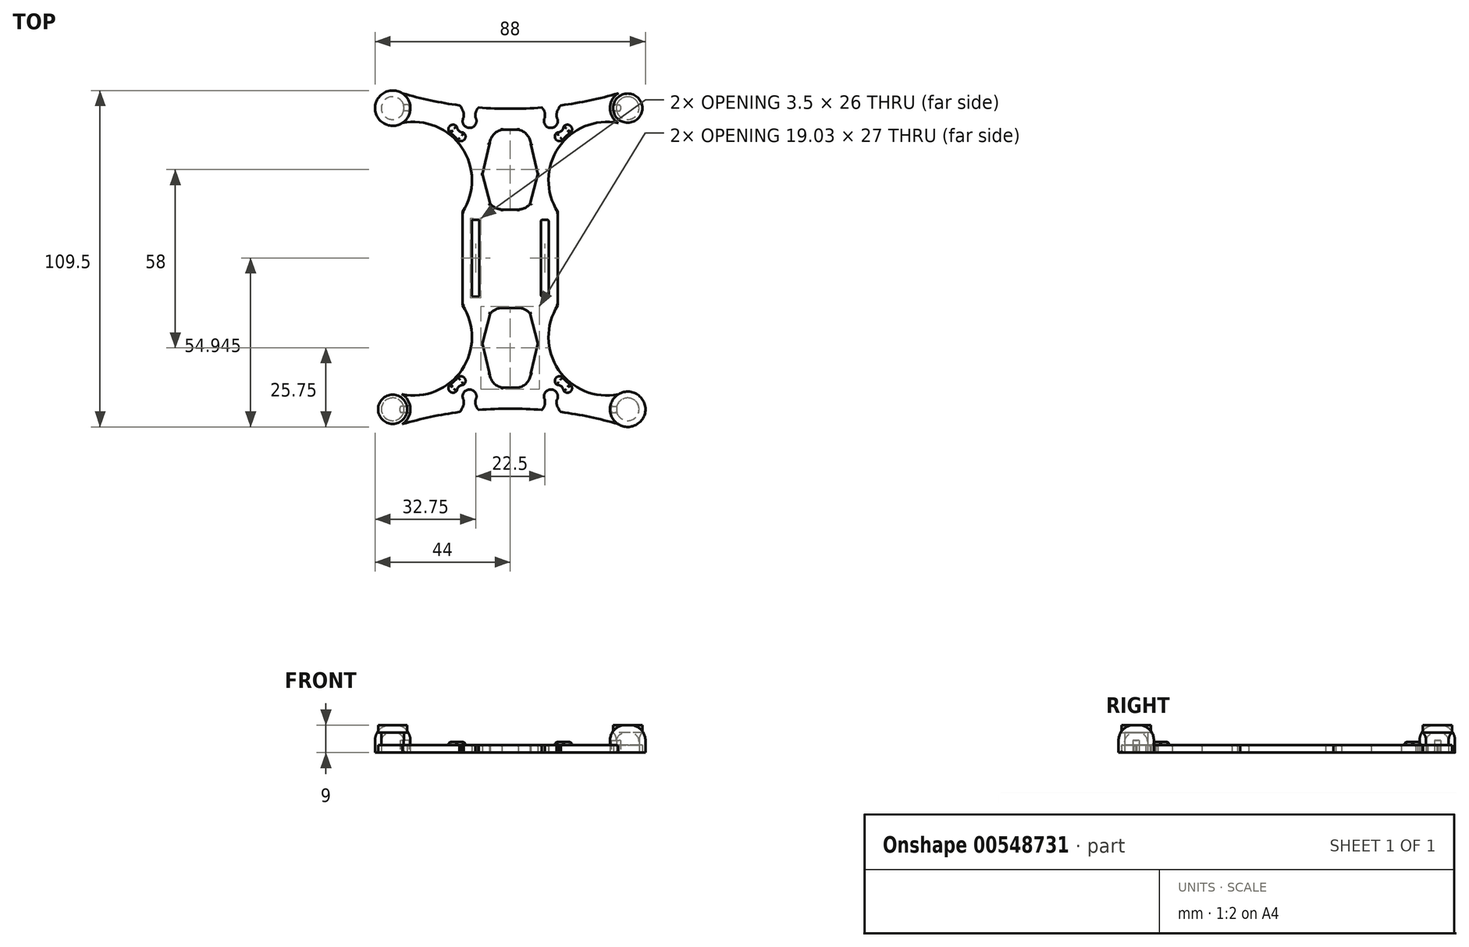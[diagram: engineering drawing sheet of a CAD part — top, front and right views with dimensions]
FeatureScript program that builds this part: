
annotation { "Feature Type Name" : "Feature", "Feature Type Description" : "" }
export const myFeature = defineFeature(function(context is Context, id is Id, definition is map)
    precondition{}
    {
        {
            assignVariable(context, id + "F0", {"name" : "FrameHeight", "anyValue" : 2.5});
        }
        {
            var Q0;
            Q0=qCreatedBy(makeId("Top.planeOp"),FACE);
            var sketch = newSketch(context, id + "F1", { "sketchPlane" : qUnion([Q0])});
            skPoint(sketch, "E0.middle", {"position": v(0, 0) * mm});
            skCircle(sketch, "E1", {"center": v(-38.25, 49) * mm, "radius": 5.75 * mm});
            skCircle(sketch, "E2.MirrorC", {"center": v(38.25, 49) * mm, "radius": 5.75 * mm});
            skCircle(sketch, "E3.MirrorC", {"center": v(-38.25, -49) * mm, "radius": 5.75 * mm});
            skCircle(sketch, "E4.MirrorC", {"center": v(38.25, -49) * mm, "radius": 5.75 * mm});
            skArc(sketch, "E5", {"start": v(-35.12, 53.82) * mm, "mid": v(-25.9, 51.5) * mm, "end": v(-16.55, 49.89) * mm});
            skCircle(sketch, "E6", {"center": v(-38.25, 49) * mm, "radius": 3.7 * mm});
            skCircle(sketch, "E7.MirrorC", {"center": v(38.25, 49) * mm, "radius": 3.7 * mm});
            skCircle(sketch, "E8.MirrorC", {"center": v(38.25, -49) * mm, "radius": 3.7 * mm});
            skCircle(sketch, "E9.MirrorC", {"center": v(-38.25, -49) * mm, "radius": 3.7 * mm});
            skPoint(sketch, "E10.MirrorP", {"position": v(-9, -27.55) * mm});
            skArc(sketch, "E11.MirrorCS", {"start": v(-2.66, -42) * mm, "mid": v(-5.49, -40.33) * mm, "end": v(-6.7, -37.29) * mm});
            skArc(sketch, "E12.MirrorCS", {"start": v(-2.66, -16) * mm, "mid": v(-4.79, -16.51) * mm, "end": v(-6.5, -17.87) * mm});
            skLineSegment(sketch, "E13", {"start": v(-6.5, -17.87) * mm, "end": v(-9, -27.55) * mm});
            skLineSegment(sketch, "E14", {"start": v(-6.7, -37.29) * mm, "end": v(-9, -27.55) * mm});
            skArc(sketch, "E15.MirrorCS", {"start": v(2.66, -16) * mm, "mid": v(4.79, -16.51) * mm, "end": v(6.5, -17.87) * mm});
            skLineSegment(sketch, "E16.MirrorCS", {"start": v(6.5, -17.87) * mm, "end": v(9, -27.55) * mm});
            skLineSegment(sketch, "E17.MirrorCS", {"start": v(6.7, -37.29) * mm, "end": v(9, -27.55) * mm});
            skArc(sketch, "E18.MirrorCS", {"start": v(2.66, -42) * mm, "mid": v(5.49, -40.33) * mm, "end": v(6.7, -37.29) * mm});
            skLineSegment(sketch, "E19", {"start": v(-2.66, -16) * mm, "end": v(2.66, -16) * mm});
            skLineSegment(sketch, "E20", {"start": v(2.66, -42) * mm, "end": v(-2.66, -42) * mm});
            skLineSegment(sketch, "E21.MirrorCS", {"start": v(-2.66, 16) * mm, "end": v(2.66, 16) * mm});
            skArc(sketch, "E22.MirrorCS", {"start": v(-2.66, 16) * mm, "mid": v(-4.79, 16.51) * mm, "end": v(-6.5, 17.87) * mm});
            skLineSegment(sketch, "E23.MirrorCS", {"start": v(-6.5, 17.87) * mm, "end": v(-9, 27.55) * mm});
            skArc(sketch, "E24.MirrorCS", {"start": v(2.66, 16) * mm, "mid": v(4.79, 16.51) * mm, "end": v(6.5, 17.87) * mm});
            skLineSegment(sketch, "E25.MirrorCS", {"start": v(6.5, 17.87) * mm, "end": v(9, 27.55) * mm});
            skLineSegment(sketch, "E26.MirrorCS", {"start": v(-6.7, 37.29) * mm, "end": v(-9, 27.55) * mm});
            skLineSegment(sketch, "E27.MirrorCS", {"start": v(6.7, 37.29) * mm, "end": v(9, 27.55) * mm});
            skArc(sketch, "E28.MirrorCS", {"start": v(2.66, 42) * mm, "mid": v(5.49, 40.33) * mm, "end": v(6.7, 37.29) * mm});
            skLineSegment(sketch, "E29.MirrorCS", {"start": v(2.66, 42) * mm, "end": v(-2.66, 42) * mm});
            skArc(sketch, "E30.MirrorCS", {"start": v(-2.66, 42) * mm, "mid": v(-5.49, 40.33) * mm, "end": v(-6.7, 37.29) * mm});
            skArc(sketch, "E31", {"start": v(-15.5, 15.2) * mm, "mid": v(-15.74, 36.19) * mm, "end": v(-35.17, 44.14) * mm});
            skArc(sketch, "E32.MirrorCS", {"start": v(-35.12, -53.82) * mm, "mid": v(-25.9, -51.5) * mm, "end": v(-16.55, -49.89) * mm});
            skArc(sketch, "E33.MirrorCS", {"start": v(15.5, 15.2) * mm, "mid": v(15.74, 36.19) * mm, "end": v(35.17, 44.14) * mm});
            skArc(sketch, "E34.MirrorCS", {"start": v(15.5, -15.2) * mm, "mid": v(15.74, -36.19) * mm, "end": v(35.17, -44.14) * mm});
            skArc(sketch, "E35.MirrorCS", {"start": v(-15.5, -15.2) * mm, "mid": v(-15.74, -36.19) * mm, "end": v(-35.17, -44.14) * mm});
            skLineSegment(sketch, "E36", {"start": v(-15.5, -15.2) * mm, "end": v(-15.5, 15.2) * mm});
            skLineSegment(sketch, "E37.bottom", {"start": v(-12, -12.3) * mm, "end": v(-10.5, -12.3) * mm});
            skLineSegment(sketch, "E37.top", {"start": v(-12, 12.7) * mm, "end": v(-10.5, 12.7) * mm});
            skLineSegment(sketch, "E37.left", {"start": v(-12.5, -11.8) * mm, "end": v(-12.5, 12.2) * mm});
            skLineSegment(sketch, "E37.right", {"start": v(-10, -11.8) * mm, "end": v(-10, 12.2) * mm});
            skLineSegment(sketch, "E38", {"start": v(-15.5, 15.2) * mm, "end": v(15.5, 15.2) * mm, "construction": true});
            skPoint(sketch, "E39.visualSharp", {"position": v(-10, -12.3) * mm});
            skArc(sketch, "E39.filletArc", {"start": v(-10.5, -12.3) * mm, "mid": v(-10.15, -12.16) * mm, "end": v(-10, -11.8) * mm});
            skPoint(sketch, "E40.visualSharp", {"position": v(-12.5, -12.3) * mm});
            skArc(sketch, "E40.filletArc", {"start": v(-12.5, -11.8) * mm, "mid": v(-12.35, -12.16) * mm, "end": v(-12, -12.3) * mm});
            skPoint(sketch, "E41.visualSharp", {"position": v(-10, 12.7) * mm});
            skArc(sketch, "E41.filletArc", {"start": v(-10, 12.2) * mm, "mid": v(-10.15, 12.55) * mm, "end": v(-10.5, 12.7) * mm});
            skPoint(sketch, "E42.visualSharp", {"position": v(-12.5, 12.7) * mm});
            skArc(sketch, "E42.filletArc", {"start": v(-12, 12.7) * mm, "mid": v(-12.35, 12.55) * mm, "end": v(-12.5, 12.2) * mm});
            skLineSegment(sketch, "E43.MirrorCS", {"start": v(12, -12.3) * mm, "end": v(10.5, -12.3) * mm});
            skArc(sketch, "E44.MirrorCS", {"start": v(12.5, -11.8) * mm, "mid": v(12.35, -12.16) * mm, "end": v(12, -12.3) * mm});
            skArc(sketch, "E45.MirrorCS", {"start": v(10.5, -12.3) * mm, "mid": v(10.15, -12.16) * mm, "end": v(10, -11.8) * mm});
            skLineSegment(sketch, "E46.MirrorCS", {"start": v(10, -11.8) * mm, "end": v(10, 12.2) * mm});
            skLineSegment(sketch, "E47.MirrorCS", {"start": v(12.5, -11.8) * mm, "end": v(12.5, 12.2) * mm});
            skArc(sketch, "E48.MirrorCS", {"start": v(10, 12.2) * mm, "mid": v(10.15, 12.55) * mm, "end": v(10.5, 12.7) * mm});
            skLineSegment(sketch, "E49.MirrorCS", {"start": v(12, 12.7) * mm, "end": v(10.5, 12.7) * mm});
            skArc(sketch, "E50.MirrorCS", {"start": v(12, 12.7) * mm, "mid": v(12.35, 12.55) * mm, "end": v(12.5, 12.2) * mm});
            skLineSegment(sketch, "E51", {"start": v(15.5, 15.2) * mm, "end": v(15.5, -15.2) * mm});
            skArc(sketch, "E52.trimOffspring", {"start": v(-10.28, 49.21) * mm, "mid": v(0, 48.79) * mm, "end": v(10.28, 49.21) * mm});
            skArc(sketch, "E53", {"start": v(-15.18, 45.95) * mm, "mid": v(-13.3, 42.57) * mm, "end": v(-11.24, 45.85) * mm});
            skArc(sketch, "E54", {"start": v(-15.18, 45.95) * mm, "mid": v(-15.18, 47.49) * mm, "end": v(-15.83, 48.88) * mm});
            skArc(sketch, "E55.MirrorCS", {"start": v(-11.24, 45.85) * mm, "mid": v(-11.2, 47.66) * mm, "end": v(-10.28, 49.21) * mm});
            skArc(sketch, "E56.trimOffspring", {"start": v(16.55, 49.89) * mm, "mid": v(25.9, 51.5) * mm, "end": v(35.12, 53.82) * mm});
            skArc(sketch, "E57.trimOffspring", {"start": v(-10.28, -49.21) * mm, "mid": v(0, -48.79) * mm, "end": v(10.28, -49.21) * mm});
            skArc(sketch, "E58.trimOffspring", {"start": v(16.55, -49.89) * mm, "mid": v(25.9, -51.5) * mm, "end": v(35.12, -53.82) * mm});
            skArc(sketch, "E59.MirrorCS", {"start": v(11.24, 45.85) * mm, "mid": v(11.2, 47.66) * mm, "end": v(10.28, 49.21) * mm});
            skArc(sketch, "E60.MirrorCS", {"start": v(15.18, 45.95) * mm, "mid": v(15.18, 47.49) * mm, "end": v(15.83, 48.88) * mm});
            skArc(sketch, "E61.MirrorCS", {"start": v(15.18, 45.95) * mm, "mid": v(13.3, 42.57) * mm, "end": v(11.24, 45.85) * mm});
            skArc(sketch, "E62.MirrorCS", {"start": v(15.18, -45.95) * mm, "mid": v(13.3, -42.57) * mm, "end": v(11.24, -45.85) * mm});
            skArc(sketch, "E63.MirrorCS", {"start": v(11.24, -45.85) * mm, "mid": v(11.2, -47.66) * mm, "end": v(10.28, -49.21) * mm});
            skArc(sketch, "E64.MirrorCS", {"start": v(15.18, -45.95) * mm, "mid": v(15.18, -47.49) * mm, "end": v(15.83, -48.88) * mm});
            skArc(sketch, "E65.MirrorCS", {"start": v(-11.24, -45.85) * mm, "mid": v(-11.2, -47.66) * mm, "end": v(-10.28, -49.21) * mm});
            skArc(sketch, "E66.MirrorCS", {"start": v(-15.18, -45.95) * mm, "mid": v(-15.18, -47.49) * mm, "end": v(-15.83, -48.88) * mm});
            skArc(sketch, "E67.MirrorCS", {"start": v(-15.18, -45.95) * mm, "mid": v(-13.3, -42.57) * mm, "end": v(-11.24, -45.85) * mm});
            skLineSegment(sketch, "E68", {"start": v(-38.25, 49) * mm, "end": v(38.25, 49) * mm, "construction": true});
            skArc(sketch, "E69", {"start": v(16.55, 49.89) * mm, "mid": v(16.05, 49.49) * mm, "end": v(15.83, 48.88) * mm});
            skArc(sketch, "E70.MirrorCS", {"start": v(-16.55, 49.89) * mm, "mid": v(-16.05, 49.49) * mm, "end": v(-15.83, 48.88) * mm});
            skArc(sketch, "E71.MirrorCS", {"start": v(-16.55, -49.89) * mm, "mid": v(-16.05, -49.49) * mm, "end": v(-15.83, -48.88) * mm});
            skArc(sketch, "E72.MirrorCS", {"start": v(16.55, -49.89) * mm, "mid": v(16.05, -49.49) * mm, "end": v(15.83, -48.88) * mm});
            skLineSegment(sketch, "E73", {"start": v(-38.25, -49) * mm, "end": v(38.25, 49) * mm, "construction": true});
            skCircle(sketch, "E74", {"center": v(-38.25, 49) * mm, "radius": 4.75 * mm});
            skCircle(sketch, "E75.MirrorC", {"center": v(38.25, 49) * mm, "radius": 4.75 * mm});
            skCircle(sketch, "E76.MirrorC", {"center": v(38.25, -49) * mm, "radius": 4.75 * mm});
            skCircle(sketch, "E77.MirrorC", {"center": v(-38.25, -49) * mm, "radius": 4.75 * mm});
            skSolve(sketch);
        }
        {
            var Q0;
            {var subQ4=sQuery(id+"F1.wireOp",EDGE,"E5");Q0=makeQuery(id+"F1.imprint","IMPRINT",FACE,{"disambiguationData":[TD([[makeQuery(id+"F1.imprint","IMPRINT",EDGE,{"derivedFrom":subQ4}),-1.0]])]});}
            var Q1;
            Q1=makeQuery(id+"F1.imprint","IMPRINT",FACE,{"disambiguationData":[TD([[makeQuery(id+"F1.imprint","IMPRINT",EDGE,{"derivedFrom":sQuery(id+"F1.wireOp",EDGE,"E9.MirrorC")}),1.0]])]});
            var Q2;
            Q2=makeQuery(id+"F1.imprint","IMPRINT",FACE,{"disambiguationData":[TD([[makeQuery(id+"F1.imprint","IMPRINT",EDGE,{"derivedFrom":sQuery(id+"F1.wireOp",EDGE,"E8.MirrorC")}),-1.0]])]});
            var Q3;
            Q3=makeQuery(id+"F1.imprint","IMPRINT",FACE,{"disambiguationData":[TD([[makeQuery(id+"F1.imprint","IMPRINT",EDGE,{"derivedFrom":sQuery(id+"F1.wireOp",EDGE,"E6")}),-1.0]])]});
            var Q4;
            Q4=makeQuery(id+"F1.imprint","IMPRINT",FACE,{"disambiguationData":[TD([[makeQuery(id+"F1.imprint","IMPRINT",EDGE,{"derivedFrom":sQuery(id+"F1.wireOp",EDGE,"E7.MirrorC")}),1.0]])]});
            var Q5;
            {var subQ0=sQuery(id+"F1.wireOp",EDGE,"7a08c846-7200-404a-ab22-a396ae0e95b40.MirrorCS");Q5=makeQuery(id+"F1.imprint","IMPRINT",FACE,{"disambiguationData":[TD([[makeQuery(id+"F1.imprint","IMPRINT",EDGE,{"derivedFrom":subQ0}),-1.0]])]});}
            extrude(context, id + "F2", {"entities" : qUnion([Q0, Q1, Q2, Q3, Q4, Q5]), "depth" : 2.5 * mm});
        }
        {
            var Q0;
            Q0=makeQuery(id+"F1.imprint","IMPRINT",FACE,{"disambiguationData":[TD([[makeQuery(id+"F1.imprint","IMPRINT",EDGE,{"derivedFrom":sQuery(id+"F1.wireOp",EDGE,"E74")}),-1.0]])]});
            var Q1;
            Q1=makeQuery(id+"F1.imprint","IMPRINT",FACE,{"disambiguationData":[TD([[makeQuery(id+"F1.imprint","IMPRINT",EDGE,{"derivedFrom":sQuery(id+"F1.wireOp",EDGE,"E75.MirrorC")}),1.0]])]});
            var Q2;
            Q2=makeQuery(id+"F1.imprint","IMPRINT",FACE,{"disambiguationData":[TD([[makeQuery(id+"F1.imprint","IMPRINT",EDGE,{"derivedFrom":sQuery(id+"F1.wireOp",EDGE,"E77.MirrorC")}),1.0]])]});
            var Q3;
            Q3=makeQuery(id+"F1.imprint","IMPRINT",FACE,{"disambiguationData":[TD([[makeQuery(id+"F1.imprint","IMPRINT",EDGE,{"derivedFrom":sQuery(id+"F1.wireOp",EDGE,"E76.MirrorC")}),-1.0]])]});
            extrude(context, id + "F3", {"entities" : qUnion([Q0, Q1, Q2, Q3]), "operationType" : NewBodyOperationType.ADD, "depth" : 3 * mm});
        }
        {
            var Q0;
            Q0=makeQuery(id+"F1.imprint","IMPRINT",FACE,{"disambiguationData":[TD([[makeQuery(id+"F1.imprint","IMPRINT",EDGE,{"derivedFrom":sQuery(id+"F1.wireOp",EDGE,"E6")}),-1.0]])]});
            var Q1;
            Q1=makeQuery(id+"F1.imprint","IMPRINT",FACE,{"disambiguationData":[TD([[makeQuery(id+"F1.imprint","IMPRINT",EDGE,{"derivedFrom":sQuery(id+"F1.wireOp",EDGE,"E7.MirrorC")}),1.0]])]});
            var Q2;
            Q2=makeQuery(id+"F1.imprint","IMPRINT",FACE,{"disambiguationData":[TD([[makeQuery(id+"F1.imprint","IMPRINT",EDGE,{"derivedFrom":sQuery(id+"F1.wireOp",EDGE,"E9.MirrorC")}),1.0]])]});
            var Q3;
            Q3=makeQuery(id+"F1.imprint","IMPRINT",FACE,{"disambiguationData":[TD([[makeQuery(id+"F1.imprint","IMPRINT",EDGE,{"derivedFrom":sQuery(id+"F1.wireOp",EDGE,"E8.MirrorC")}),-1.0]])]});
            var Q4;
            Q4=makeQuery(id+"F1.imprint","IMPRINT",FACE,{"disambiguationData":[TD([[makeQuery(id+"F1.imprint","IMPRINT",EDGE,{"derivedFrom":sQuery(id+"F1.wireOp",EDGE,"E6")}),1.0]])]});
            var Q5;
            Q5=makeQuery(id+"F1.imprint","IMPRINT",FACE,{"disambiguationData":[TD([[makeQuery(id+"F1.imprint","IMPRINT",EDGE,{"derivedFrom":sQuery(id+"F1.wireOp",EDGE,"E7.MirrorC")}),-1.0]])]});
            var Q6;
            Q6=makeQuery(id+"F1.imprint","IMPRINT",FACE,{"disambiguationData":[TD([[makeQuery(id+"F1.imprint","IMPRINT",EDGE,{"derivedFrom":sQuery(id+"F1.wireOp",EDGE,"E8.MirrorC")}),1.0]])]});
            var Q7;
            Q7=makeQuery(id+"F1.imprint","IMPRINT",FACE,{"disambiguationData":[TD([[makeQuery(id+"F1.imprint","IMPRINT",EDGE,{"derivedFrom":sQuery(id+"F1.wireOp",EDGE,"E9.MirrorC")}),-1.0]])]});
            var Q8;
            {var subQ0=sQuery(id+"F1.wireOp",EDGE,"ea4f1012-2509-42ab-b6be-2330c5534f0a0.MirrorCS");var subQ1=sQuery(id+"F1.wireOp",EDGE,"cdfdab9b-bf2e-43ec-8392-f97786d2ea0d0.MirrorCS");var subQ2=sQuery(id+"F1.wireOp",EDGE,"465e94d3-5aed-43b1-ab28-4905a897ac150.MirrorCS");var subQ3=sQuery(id+"F1.wireOp",EDGE,"98a759bb-2186-4722-986c-5ad8236f98b60.MirrorCS");var subQ4=sQuery(id+"F1.wireOp",EDGE,"529e4913-d2e2-4b9c-8764-fd74a515156b0.MirrorCS");var subQ5=sQuery(id+"F1.wireOp",EDGE,"a75351e4-8b9f-4b28-a4a3-4962784478ad0.MirrorCS");var subQ6=sQuery(id+"F1.wireOp",EDGE,"82538637-7302-4e28-b2d0-c30d791653240.MirrorCS");var subQ7=sQuery(id+"F1.wireOp",EDGE,"56e68159-8ace-49cd-9e0b-4dd6a05a3e180.MirrorCS");var subQ8=sQuery(id+"F1.wireOp",EDGE,"e7e79bb3-8a2c-4938-af19-8f637f7eba370.MirrorCS");var subQ9=sQuery(id+"F1.wireOp",EDGE,"2316bcf3-3be9-4e9e-b8e2-497a6a1952b90.MirrorCS");var subQ10=sQuery(id+"F1.wireOp",EDGE,"1773aba8-4819-4f46-a8a7-8d94881a3e2a0.MirrorCS");var subQ11=sQuery(id+"F1.wireOp",EDGE,"e0e34dce-b0e1-4d64-a790-8c4829cf73b10.MirrorCS");var subQ12=sQuery(id+"F1.wireOp",EDGE,"8cd6d0e1-198d-4ddf-9674-687771b3d4800.MirrorCS");var subQ13=sQuery(id+"F1.wireOp",EDGE,"258af2fb-57e0-4cd8-8c30-8cafca4a9de30.MirrorCS");var subQ14=sQuery(id+"F1.wireOp",EDGE,"a07b8381-fd63-4e58-856e-6aaff1297d55.filletArc");var subQ15=sQuery(id+"F1.wireOp",EDGE,"RvagwD08-4saL-jRzY-J36Z-niyVwtinKrBz");var subQ16=sQuery(id+"F1.wireOp",EDGE,"o4VfrY1E-f77m-jJ6D-3hSz-oWbsnZmPJ7RM");var subQ17=sQuery(id+"F1.wireOp",EDGE,"5SzH9PIc-MBC3-JWxo-jWJ1-gy0vg8dHxIne");var subQ18=sQuery(id+"F1.wireOp",EDGE,"Skl9KyDn-OFwj-jcuM-sPno-qYqNKXC7fZA3");var subQ19=sQuery(id+"F1.wireOp",EDGE,"5RGUndvU-jcMW-WSWi-Bxv8-2VV6o0UGLXlU");var subQ20=sQuery(id+"F1.wireOp",EDGE,"NKQneA6F-sO9O-ycv6-QC4M-7Sw9j2aKeUUz");var subQ21=sQuery(id+"F1.wireOp",EDGE,"41db651c-dc80-447a-ac2a-c1855a6981c0.filletArc");var subQ22=sQuery(id+"F1.wireOp",EDGE,"cd34b8fd-3b9d-40b5-866b-1931df3bf95f.filletArc");var subQ23=sQuery(id+"F1.wireOp",EDGE,"e2ad8a51-9023-4a85-890f-8adf256902f4.filletArc");var subQ24=sQuery(id+"F1.wireOp",EDGE,"f659aba6-3ceb-4f67-afd8-6bc25f8b2d52.filletArc");var subQ25=sQuery(id+"F1.wireOp",EDGE,"E30.MirrorCS");var subQ26=sQuery(id+"F1.wireOp",EDGE,"E29.MirrorCS");var subQ27=sQuery(id+"F1.wireOp",EDGE,"E28.MirrorCS");var subQ28=sQuery(id+"F1.wireOp",EDGE,"E27.MirrorCS");var subQ29=sQuery(id+"F1.wireOp",EDGE,"E26.MirrorCS");var subQ30=sQuery(id+"F1.wireOp",EDGE,"E25.MirrorCS");var subQ31=sQuery(id+"F1.wireOp",EDGE,"E24.MirrorCS");var subQ32=sQuery(id+"F1.wireOp",EDGE,"E23.MirrorCS");var subQ33=sQuery(id+"F1.wireOp",EDGE,"E22.MirrorCS");var subQ34=sQuery(id+"F1.wireOp",EDGE,"E21.MirrorCS");var subQ35=sQuery(id+"F1.wireOp",EDGE,"E20");var subQ36=sQuery(id+"F1.wireOp",EDGE,"E19");var subQ37=sQuery(id+"F1.wireOp",EDGE,"E18.MirrorCS");var subQ38=sQuery(id+"F1.wireOp",EDGE,"E17.MirrorCS");var subQ39=sQuery(id+"F1.wireOp",EDGE,"E16.MirrorCS");var subQ40=sQuery(id+"F1.wireOp",EDGE,"E15.MirrorCS");var subQ41=sQuery(id+"F1.wireOp",EDGE,"E14");var subQ42=sQuery(id+"F1.wireOp",EDGE,"E13");var subQ43=sQuery(id+"F1.wireOp",EDGE,"E12.MirrorCS");var subQ44=sQuery(id+"F1.wireOp",EDGE,"E11.MirrorCS");var subQ45=sQuery(id+"F1.wireOp",EDGE,"8O0KtBdD-sCAZ-nUyN-ZE4b-Pr8atPqkOLOt.right");var subQ46=sQuery(id+"F1.wireOp",EDGE,"8O0KtBdD-sCAZ-nUyN-ZE4b-Pr8atPqkOLOt.top");var subQ47=sQuery(id+"F1.wireOp",EDGE,"8O0KtBdD-sCAZ-nUyN-ZE4b-Pr8atPqkOLOt.bottom");var subQ48=sQuery(id+"F1.wireOp",EDGE,"3a3e3443-e76c-4b3f-931a-bba0a9ca54bb0.MirrorC");var subQ49=sQuery(id+"F1.wireOp",EDGE,"5ae8c34d-aa19-45d0-b816-4b0481c35e6e0.MirrorC");var subQ50=sQuery(id+"F1.wireOp",EDGE,"e54bd452-817c-44b1-b4a1-4a82a5b737490.MirrorC");var subQ51=sQuery(id+"F1.wireOp",EDGE,"vB4YpJxw-nM1r-KAMU-Z2z7-AA1Xbjjr12VQ");var subQ52=sQuery(id+"F1.wireOp",EDGE,"2126723b-73e3-4daa-88ad-461916ae88fc0.MirrorCS");var subQ53=sQuery(id+"F1.wireOp",EDGE,"8d91ff8a-54ff-47bb-bb8d-6ed09a5a66a50.MirrorCS");var subQ54=sQuery(id+"F1.wireOp",EDGE,"462311f5-9079-46a5-b6e4-7ace82524d020.MirrorCS");var subQ55=sQuery(id+"F1.wireOp",EDGE,"8mwgoKQL-uejJ-Ytzu-yeJP-nfI78MkwDY2L");var subQ56=sQuery(id+"F1.wireOp",EDGE,"3589fe97-52ff-42bc-b7a9-5f631560aecf0.MirrorCS");var subQ57=sQuery(id+"F1.wireOp",EDGE,"E5");var subQ58=sQuery(id+"F1.wireOp",EDGE,"E4.MirrorC");var subQ59=sQuery(id+"F1.wireOp",EDGE,"E3.MirrorC");var subQ60=sQuery(id+"F1.wireOp",EDGE,"E2.MirrorC");var subQ61=sQuery(id+"F1.wireOp",EDGE,"E1");Q8=makeQuery(id+"FTKf5rjYO4gTYV3_1.boolean.opBoolean","MERGE",FACE,{"derivedFrom":[makeQuery(id+"FOrR15PyCScxact_0.opExtrude","CAP_FACE",FACE,{"disambiguationData":[OSD([subQ61,subQ60,subQ59,subQ58,subQ57,subQ56,subQ55,subQ54,subQ53,subQ52,subQ51,subQ50,subQ49,subQ48,subQ47,subQ46,subQ45,subQ44,subQ43,subQ42,subQ41,subQ40,subQ39,subQ38,subQ37,subQ36,subQ35,subQ34,subQ33,subQ32,subQ31,subQ30,subQ29,subQ28,subQ27,subQ26,subQ25,subQ24,subQ23,subQ22,subQ21,subQ20,subQ19,subQ18,subQ17,subQ16,subQ15,subQ14,subQ13,subQ12,subQ11,subQ10,subQ9,subQ8,subQ7,subQ6,subQ5,subQ4,subQ3,subQ2,subQ1,subQ0])],"isStart":false}),makeQuery(id+"FTKf5rjYO4gTYV3_1.opExtrude","CAP_FACE",FACE,{"disambiguationData":[OSD([subQ61,subQ60,subQ59,subQ58,subQ57,subQ56,sQuery(id+"F1.wireOp",EDGE,"E6"),subQ55,subQ54,subQ53,subQ52,sQuery(id+"F1.wireOp",EDGE,"E7.MirrorC"),sQuery(id+"F1.wireOp",EDGE,"E8.MirrorC"),sQuery(id+"F1.wireOp",EDGE,"E9.MirrorC"),subQ51,subQ50,subQ49,subQ48,subQ47,subQ46,subQ45,subQ44,subQ43,subQ42,subQ41,subQ40,subQ39,subQ38,subQ37,subQ36,subQ35,subQ34,subQ33,subQ32,subQ31,subQ30,subQ29,subQ28,subQ27,subQ26,subQ25,subQ24,subQ23,subQ22,subQ21,subQ20,subQ19,subQ18,subQ17,subQ16,subQ15,subQ14,subQ13,subQ12,subQ11,subQ10,subQ9,subQ8,subQ7,subQ6,subQ5,subQ4,subQ3,subQ2,subQ1,subQ0])],"isStart":false})]});}
            var Q9;
            Q9=makeQuery(id+"FOrR15PyCScxact_0.opExtrude","SWEPT_BODY",BODY,{"disambiguationData":[OSD([sQuery(id+"F1.wireOp",EDGE,"E1"),sQuery(id+"F1.wireOp",EDGE,"E2.MirrorC"),sQuery(id+"F1.wireOp",EDGE,"E3.MirrorC"),sQuery(id+"F1.wireOp",EDGE,"E4.MirrorC"),sQuery(id+"F1.wireOp",EDGE,"E5"),sQuery(id+"F1.wireOp",EDGE,"3589fe97-52ff-42bc-b7a9-5f631560aecf0.MirrorCS"),sQuery(id+"F1.wireOp",EDGE,"8mwgoKQL-uejJ-Ytzu-yeJP-nfI78MkwDY2L"),sQuery(id+"F1.wireOp",EDGE,"462311f5-9079-46a5-b6e4-7ace82524d020.MirrorCS"),sQuery(id+"F1.wireOp",EDGE,"8d91ff8a-54ff-47bb-bb8d-6ed09a5a66a50.MirrorCS"),sQuery(id+"F1.wireOp",EDGE,"2126723b-73e3-4daa-88ad-461916ae88fc0.MirrorCS"),sQuery(id+"F1.wireOp",EDGE,"vB4YpJxw-nM1r-KAMU-Z2z7-AA1Xbjjr12VQ"),sQuery(id+"F1.wireOp",EDGE,"e54bd452-817c-44b1-b4a1-4a82a5b737490.MirrorC"),sQuery(id+"F1.wireOp",EDGE,"5ae8c34d-aa19-45d0-b816-4b0481c35e6e0.MirrorC"),sQuery(id+"F1.wireOp",EDGE,"3a3e3443-e76c-4b3f-931a-bba0a9ca54bb0.MirrorC"),sQuery(id+"F1.wireOp",EDGE,"8O0KtBdD-sCAZ-nUyN-ZE4b-Pr8atPqkOLOt.bottom"),sQuery(id+"F1.wireOp",EDGE,"8O0KtBdD-sCAZ-nUyN-ZE4b-Pr8atPqkOLOt.top"),sQuery(id+"F1.wireOp",EDGE,"8O0KtBdD-sCAZ-nUyN-ZE4b-Pr8atPqkOLOt.right"),sQuery(id+"F1.wireOp",EDGE,"E11.MirrorCS"),sQuery(id+"F1.wireOp",EDGE,"E12.MirrorCS"),sQuery(id+"F1.wireOp",EDGE,"E13"),sQuery(id+"F1.wireOp",EDGE,"E14"),sQuery(id+"F1.wireOp",EDGE,"E15.MirrorCS"),sQuery(id+"F1.wireOp",EDGE,"E16.MirrorCS"),sQuery(id+"F1.wireOp",EDGE,"E17.MirrorCS"),sQuery(id+"F1.wireOp",EDGE,"E18.MirrorCS"),sQuery(id+"F1.wireOp",EDGE,"E19"),sQuery(id+"F1.wireOp",EDGE,"E20"),sQuery(id+"F1.wireOp",EDGE,"E21.MirrorCS"),sQuery(id+"F1.wireOp",EDGE,"E22.MirrorCS"),sQuery(id+"F1.wireOp",EDGE,"E23.MirrorCS"),sQuery(id+"F1.wireOp",EDGE,"E24.MirrorCS"),sQuery(id+"F1.wireOp",EDGE,"E25.MirrorCS"),sQuery(id+"F1.wireOp",EDGE,"E26.MirrorCS"),sQuery(id+"F1.wireOp",EDGE,"E27.MirrorCS"),sQuery(id+"F1.wireOp",EDGE,"E28.MirrorCS"),sQuery(id+"F1.wireOp",EDGE,"E29.MirrorCS"),sQuery(id+"F1.wireOp",EDGE,"E30.MirrorCS"),sQuery(id+"F1.wireOp",EDGE,"f659aba6-3ceb-4f67-afd8-6bc25f8b2d52.filletArc"),sQuery(id+"F1.wireOp",EDGE,"e2ad8a51-9023-4a85-890f-8adf256902f4.filletArc"),sQuery(id+"F1.wireOp",EDGE,"cd34b8fd-3b9d-40b5-866b-1931df3bf95f.filletArc"),sQuery(id+"F1.wireOp",EDGE,"41db651c-dc80-447a-ac2a-c1855a6981c0.filletArc"),sQuery(id+"F1.wireOp",EDGE,"NKQneA6F-sO9O-ycv6-QC4M-7Sw9j2aKeUUz"),sQuery(id+"F1.wireOp",EDGE,"5RGUndvU-jcMW-WSWi-Bxv8-2VV6o0UGLXlU"),sQuery(id+"F1.wireOp",EDGE,"Skl9KyDn-OFwj-jcuM-sPno-qYqNKXC7fZA3"),sQuery(id+"F1.wireOp",EDGE,"5SzH9PIc-MBC3-JWxo-jWJ1-gy0vg8dHxIne"),sQuery(id+"F1.wireOp",EDGE,"o4VfrY1E-f77m-jJ6D-3hSz-oWbsnZmPJ7RM"),sQuery(id+"F1.wireOp",EDGE,"RvagwD08-4saL-jRzY-J36Z-niyVwtinKrBz"),sQuery(id+"F1.wireOp",EDGE,"a07b8381-fd63-4e58-856e-6aaff1297d55.filletArc"),sQuery(id+"F1.wireOp",EDGE,"258af2fb-57e0-4cd8-8c30-8cafca4a9de30.MirrorCS"),sQuery(id+"F1.wireOp",EDGE,"8cd6d0e1-198d-4ddf-9674-687771b3d4800.MirrorCS"),sQuery(id+"F1.wireOp",EDGE,"e0e34dce-b0e1-4d64-a790-8c4829cf73b10.MirrorCS"),sQuery(id+"F1.wireOp",EDGE,"1773aba8-4819-4f46-a8a7-8d94881a3e2a0.MirrorCS"),sQuery(id+"F1.wireOp",EDGE,"2316bcf3-3be9-4e9e-b8e2-497a6a1952b90.MirrorCS"),sQuery(id+"F1.wireOp",EDGE,"e7e79bb3-8a2c-4938-af19-8f637f7eba370.MirrorCS"),sQuery(id+"F1.wireOp",EDGE,"56e68159-8ace-49cd-9e0b-4dd6a05a3e180.MirrorCS"),sQuery(id+"F1.wireOp",EDGE,"82538637-7302-4e28-b2d0-c30d791653240.MirrorCS"),sQuery(id+"F1.wireOp",EDGE,"a75351e4-8b9f-4b28-a4a3-4962784478ad0.MirrorCS"),sQuery(id+"F1.wireOp",EDGE,"529e4913-d2e2-4b9c-8764-fd74a515156b0.MirrorCS"),sQuery(id+"F1.wireOp",EDGE,"98a759bb-2186-4722-986c-5ad8236f98b60.MirrorCS"),sQuery(id+"F1.wireOp",EDGE,"465e94d3-5aed-43b1-ab28-4905a897ac150.MirrorCS"),sQuery(id+"F1.wireOp",EDGE,"cdfdab9b-bf2e-43ec-8392-f97786d2ea0d0.MirrorCS"),sQuery(id+"F1.wireOp",EDGE,"ea4f1012-2509-42ab-b6be-2330c5534f0a0.MirrorCS")])]});
            extrude(context, id + "F4", {"entities" : qUnion([Q0, Q1, Q2, Q3, Q4, Q5, Q6, Q7]), "depth" : 9 * mm, "hasSecondDirection" : true, "secondDirectionOppositeDirection" : false, "secondDirectionBoundEntityFace" : qUnion([Q8]), "secondDirectionBoundEntityBody" : qUnion([Q9]), "secondDirectionDepth" : (getVariable(context, 'FrameHeight')) * mm});
        }
        {
            var Q0;
            Q0=makeQuery(id+"F1.imprint","IMPRINT",FACE,{"disambiguationData":[TD([[makeQuery(id+"F1.imprint","IMPRINT",EDGE,{"derivedFrom":sQuery(id+"F1.wireOp",EDGE,"E77.MirrorC")}),1.0]])]});
            var Q1;
            Q1=makeQuery(id+"F1.imprint","IMPRINT",FACE,{"disambiguationData":[TD([[makeQuery(id+"F1.imprint","IMPRINT",EDGE,{"derivedFrom":sQuery(id+"F1.wireOp",EDGE,"E74")}),-1.0]])]});
            var Q2;
            Q2=makeQuery(id+"F1.imprint","IMPRINT",FACE,{"disambiguationData":[TD([[makeQuery(id+"F1.imprint","IMPRINT",EDGE,{"derivedFrom":sQuery(id+"F1.wireOp",EDGE,"E76.MirrorC")}),-1.0]])]});
            var Q3;
            Q3=makeQuery(id+"F1.imprint","IMPRINT",FACE,{"disambiguationData":[TD([[makeQuery(id+"F1.imprint","IMPRINT",EDGE,{"derivedFrom":sQuery(id+"F1.wireOp",EDGE,"E75.MirrorC")}),1.0]])]});
            extrude(context, id + "F5", {"entities" : qUnion([Q0, Q1, Q2, Q3]), "operationType" : NewBodyOperationType.ADD, "depth" : 9 * mm, "hasSecondDirection" : true, "secondDirectionOppositeDirection" : false, "secondDirectionDepth" : 3 * mm});
        }
        {
            var Q0;
            Q0=makeQuery(id+"F1.imprint","IMPRINT",FACE,{"disambiguationData":[TD([[makeQuery(id+"F1.imprint","IMPRINT",EDGE,{"derivedFrom":sQuery(id+"F1.wireOp",EDGE,"E6")}),1.0]])]});
            var Q1;
            Q1=makeQuery(id+"F1.imprint","IMPRINT",FACE,{"disambiguationData":[TD([[makeQuery(id+"F1.imprint","IMPRINT",EDGE,{"derivedFrom":sQuery(id+"F1.wireOp",EDGE,"E7.MirrorC")}),-1.0]])]});
            var Q2;
            Q2=makeQuery(id+"F1.imprint","IMPRINT",FACE,{"disambiguationData":[TD([[makeQuery(id+"F1.imprint","IMPRINT",EDGE,{"derivedFrom":sQuery(id+"F1.wireOp",EDGE,"E9.MirrorC")}),-1.0]])]});
            var Q3;
            Q3=makeQuery(id+"F1.imprint","IMPRINT",FACE,{"disambiguationData":[TD([[makeQuery(id+"F1.imprint","IMPRINT",EDGE,{"derivedFrom":sQuery(id+"F1.wireOp",EDGE,"E8.MirrorC")}),1.0]])]});
            extrude(context, id + "F6", {"entities" : qUnion([Q0, Q1, Q2, Q3]), "operationType" : NewBodyOperationType.REMOVE, "depth" : 6.5 * mm, "hasSecondDirection" : true, "secondDirectionOppositeDirection" : false, "secondDirectionDepth" : 2.5 * mm});
        }
        {
            var Q0;
            Q0=makeQuery(id+"F5.opExtrude","CAP_EDGE",EDGE,{"disambiguationData":[OSD([sQuery(id+"F1.wireOp",EDGE,"E1")])],"isStart":false});
            var Q1;
            Q1=makeQuery(id+"F5.opExtrude","CAP_EDGE",EDGE,{"disambiguationData":[OSD([sQuery(id+"F1.wireOp",EDGE,"E2.MirrorC")])],"isStart":false});
            var Q2;
            Q2=makeQuery(id+"F5.opExtrude","CAP_EDGE",EDGE,{"disambiguationData":[OSD([sQuery(id+"F1.wireOp",EDGE,"E4.MirrorC")])],"isStart":false});
            var Q3;
            Q3=makeQuery(id+"F5.opExtrude","CAP_EDGE",EDGE,{"disambiguationData":[OSD([sQuery(id+"F1.wireOp",EDGE,"E3.MirrorC")])],"isStart":false});
            fillet(context, id + "F7", {"entities" : qUnion([Q0, Q1, Q2, Q3]), "radius" : 5 * mm, "tangentPropagation" : true, "allowEdgeOverflow" : false});
        }
        {
            var Q0;
            Q0=makeQuery(id+"F6.boolean.opBoolean","COPY",EDGE,{"derivedFrom":makeQuery(id+"F6.opExtrude","CAP_EDGE",EDGE,{"disambiguationData":[OSD([sQuery(id+"F1.wireOp",EDGE,"E6")])],"isStart":false})});
            var Q1;
            Q1=makeQuery(id+"F6.boolean.opBoolean","COPY",EDGE,{"derivedFrom":makeQuery(id+"F6.opExtrude","CAP_EDGE",EDGE,{"disambiguationData":[OSD([sQuery(id+"F1.wireOp",EDGE,"E7.MirrorC")])],"isStart":false})});
            var Q2;
            Q2=makeQuery(id+"F6.boolean.opBoolean","COPY",FACE,{"derivedFrom":makeQuery(id+"F6.opExtrude","CAP_FACE",FACE,{"disambiguationData":[OSD([sQuery(id+"F1.wireOp",EDGE,"E8.MirrorC")])],"isStart":false})});
            var Q3;
            Q3=makeQuery(id+"F6.boolean.opBoolean","COPY",FACE,{"derivedFrom":makeQuery(id+"F6.opExtrude","CAP_FACE",FACE,{"disambiguationData":[OSD([sQuery(id+"F1.wireOp",EDGE,"E9.MirrorC")])],"isStart":false})});
            fillet(context, id + "F8", {"entities" : qUnion([Q0, Q1, Q2, Q3]), "radius" : 3 * mm, "tangentPropagation" : true, "allowEdgeOverflow" : false});
        }
        {
            var Q0;
            Q0=makeQuery(id+"F1.imprint","IMPRINT",FACE,{"disambiguationData":[TD([[makeQuery(id+"F1.imprint","IMPRINT",EDGE,{"derivedFrom":sQuery(id+"F1.wireOp",EDGE,"E6")}),-1.0]])]});
            var sketch = newSketch(context, id + "F9", { "sketchPlane" : qUnion([Q0])});
            skLineSegment(sketch, "E78.bottom", {"start": v(-33.4, 50.05) * mm, "end": v(-35.4, 50.05) * mm});
            skLineSegment(sketch, "E78.top", {"start": v(-33.4, 48.05) * mm, "end": v(-35.4, 48.05) * mm});
            skLineSegment(sketch, "E78.left", {"start": v(-32.9, 49.55) * mm, "end": v(-32.9, 48.55) * mm});
            skLineSegment(sketch, "E78.right", {"start": v(-35.9, 49.55) * mm, "end": v(-35.9, 48.55) * mm});
            skPoint(sketch, "E78.middle", {"position": v(-34.4, 49.05) * mm});
            skPoint(sketch, "E79.visualSharp", {"position": v(-32.9, 50.05) * mm});
            skArc(sketch, "E79.filletArc", {"start": v(-32.9, 49.55) * mm, "mid": v(-33.05, 49.9) * mm, "end": v(-33.4, 50.05) * mm});
            skPoint(sketch, "E80.visualSharp", {"position": v(-32.9, 48.05) * mm});
            skArc(sketch, "E80.filletArc", {"start": v(-33.4, 48.05) * mm, "mid": v(-33.05, 48.2) * mm, "end": v(-32.9, 48.55) * mm});
            skPoint(sketch, "E81.visualSharp", {"position": v(-35.9, 48.05) * mm});
            skArc(sketch, "E81.filletArc", {"start": v(-35.9, 48.55) * mm, "mid": v(-35.75, 48.2) * mm, "end": v(-35.4, 48.05) * mm});
            skPoint(sketch, "E82.visualSharp", {"position": v(-35.9, 50.05) * mm});
            skArc(sketch, "E82.filletArc", {"start": v(-35.4, 50.05) * mm, "mid": v(-35.75, 49.9) * mm, "end": v(-35.9, 49.55) * mm});
            skLineSegment(sketch, "E83.MirrorCS", {"start": v(33.4, 48.05) * mm, "end": v(35.4, 48.05) * mm});
            skLineSegment(sketch, "E84.MirrorCS", {"start": v(35.9, 49.55) * mm, "end": v(35.9, 48.55) * mm});
            skLineSegment(sketch, "E85.MirrorCS", {"start": v(33.4, 50.05) * mm, "end": v(35.4, 50.05) * mm});
            skLineSegment(sketch, "E86.MirrorCS", {"start": v(32.9, 49.55) * mm, "end": v(32.9, 48.55) * mm});
            skArc(sketch, "E87.MirrorCS", {"start": v(32.9, 49.55) * mm, "mid": v(33.05, 49.9) * mm, "end": v(33.4, 50.05) * mm});
            skArc(sketch, "E88.MirrorCS", {"start": v(33.4, 48.05) * mm, "mid": v(33.05, 48.2) * mm, "end": v(32.9, 48.55) * mm});
            skArc(sketch, "E89.MirrorCS", {"start": v(35.9, 48.55) * mm, "mid": v(35.75, 48.2) * mm, "end": v(35.4, 48.05) * mm});
            skArc(sketch, "E90.MirrorCS", {"start": v(35.4, 50.05) * mm, "mid": v(35.75, 49.9) * mm, "end": v(35.9, 49.55) * mm});
            skLineSegment(sketch, "E91.MirrorCS", {"start": v(33.4, -48.05) * mm, "end": v(35.4, -48.05) * mm});
            skLineSegment(sketch, "E92.MirrorCS", {"start": v(33.4, -50.05) * mm, "end": v(35.4, -50.05) * mm});
            skLineSegment(sketch, "E93.MirrorCS", {"start": v(32.9, -49.55) * mm, "end": v(32.9, -48.55) * mm});
            skLineSegment(sketch, "E94.MirrorCS", {"start": v(35.9, -49.55) * mm, "end": v(35.9, -48.55) * mm});
            skArc(sketch, "E95.MirrorCS", {"start": v(35.4, -50.05) * mm, "mid": v(35.75, -49.9) * mm, "end": v(35.9, -49.55) * mm});
            skArc(sketch, "E96.MirrorCS", {"start": v(32.9, -49.55) * mm, "mid": v(33.05, -49.9) * mm, "end": v(33.4, -50.05) * mm});
            skArc(sketch, "E97.MirrorCS", {"start": v(33.4, -48.05) * mm, "mid": v(33.05, -48.2) * mm, "end": v(32.9, -48.55) * mm});
            skArc(sketch, "E98.MirrorCS", {"start": v(35.9, -48.55) * mm, "mid": v(35.75, -48.2) * mm, "end": v(35.4, -48.05) * mm});
            skLineSegment(sketch, "E99.MirrorCS", {"start": v(-33.4, -48.05) * mm, "end": v(-35.4, -48.05) * mm});
            skArc(sketch, "E100.MirrorCS", {"start": v(-35.9, -48.55) * mm, "mid": v(-35.75, -48.2) * mm, "end": v(-35.4, -48.05) * mm});
            skLineSegment(sketch, "E101.MirrorCS", {"start": v(-35.9, -49.55) * mm, "end": v(-35.9, -48.55) * mm});
            skArc(sketch, "E102.MirrorCS", {"start": v(-35.4, -50.05) * mm, "mid": v(-35.75, -49.9) * mm, "end": v(-35.9, -49.55) * mm});
            skLineSegment(sketch, "E103.MirrorCS", {"start": v(-33.4, -50.05) * mm, "end": v(-35.4, -50.05) * mm});
            skArc(sketch, "E104.MirrorCS", {"start": v(-32.9, -49.55) * mm, "mid": v(-33.05, -49.9) * mm, "end": v(-33.4, -50.05) * mm});
            skLineSegment(sketch, "E105.MirrorCS", {"start": v(-32.9, -49.55) * mm, "end": v(-32.9, -48.55) * mm});
            skArc(sketch, "E106.MirrorCS", {"start": v(-33.4, -48.05) * mm, "mid": v(-33.05, -48.2) * mm, "end": v(-32.9, -48.55) * mm});
            skSolve(sketch);
        }
        {
            var Q0;
            Q0=qSketchRegion(id+"F9",true);
            extrude(context, id + "F10", {"entities" : qUnion([Q0]), "operationType" : NewBodyOperationType.REMOVE, "depth" : 4 * mm});
        }
        {
            var Q0;
            Q0=makeQuery(id+"F2.opExtrude","CAP_EDGE",EDGE,{"disambiguationData":[OSD([sQuery(id+"F1.wireOp",EDGE,"E23.MirrorCS")])],"isStart":true});
            var Q1;
            Q1=makeQuery(id+"F2.opExtrude","CAP_EDGE",EDGE,{"disambiguationData":[OSD([sQuery(id+"F1.wireOp",EDGE,"E22.MirrorCS")])],"isStart":true});
            var Q2;
            Q2=makeQuery(id+"F2.opExtrude","CAP_EDGE",EDGE,{"disambiguationData":[OSD([sQuery(id+"F1.wireOp",EDGE,"E21.MirrorCS")])],"isStart":true});
            var Q3;
            Q3=makeQuery(id+"F2.opExtrude","CAP_EDGE",EDGE,{"disambiguationData":[OSD([sQuery(id+"F1.wireOp",EDGE,"E25.MirrorCS")])],"isStart":true});
            var Q4;
            Q4=makeQuery(id+"F2.opExtrude","CAP_EDGE",EDGE,{"disambiguationData":[OSD([sQuery(id+"F1.wireOp",EDGE,"E24.MirrorCS")])],"isStart":true});
            var Q5;
            Q5=makeQuery(id+"F2.opExtrude","CAP_EDGE",EDGE,{"disambiguationData":[OSD([sQuery(id+"F1.wireOp",EDGE,"E27.MirrorCS")])],"isStart":true});
            var Q6;
            Q6=makeQuery(id+"F2.opExtrude","CAP_EDGE",EDGE,{"disambiguationData":[OSD([sQuery(id+"F1.wireOp",EDGE,"E26.MirrorCS")])],"isStart":true});
            var Q7;
            Q7=makeQuery(id+"F2.opExtrude","CAP_EDGE",EDGE,{"disambiguationData":[OSD([sQuery(id+"F1.wireOp",EDGE,"E30.MirrorCS")])],"isStart":true});
            var Q8;
            Q8=makeQuery(id+"F2.opExtrude","CAP_EDGE",EDGE,{"disambiguationData":[OSD([sQuery(id+"F1.wireOp",EDGE,"E29.MirrorCS")])],"isStart":true});
            var Q9;
            Q9=makeQuery(id+"F2.opExtrude","CAP_EDGE",EDGE,{"disambiguationData":[OSD([sQuery(id+"F1.wireOp",EDGE,"E28.MirrorCS")])],"isStart":true});
            var Q10;
            Q10=makeQuery(id+"F2.opExtrude","CAP_EDGE",EDGE,{"disambiguationData":[OSD([sQuery(id+"F1.wireOp",EDGE,"E24.MirrorCS")])],"isStart":false});
            var Q11;
            Q11=makeQuery(id+"F2.opExtrude","CAP_EDGE",EDGE,{"disambiguationData":[OSD([sQuery(id+"F1.wireOp",EDGE,"E21.MirrorCS")])],"isStart":false});
            var Q12;
            Q12=makeQuery(id+"F2.opExtrude","CAP_EDGE",EDGE,{"disambiguationData":[OSD([sQuery(id+"F1.wireOp",EDGE,"E22.MirrorCS")])],"isStart":false});
            var Q13;
            Q13=makeQuery(id+"F2.opExtrude","CAP_EDGE",EDGE,{"disambiguationData":[OSD([sQuery(id+"F1.wireOp",EDGE,"E23.MirrorCS")])],"isStart":false});
            var Q14;
            Q14=makeQuery(id+"F2.opExtrude","CAP_EDGE",EDGE,{"disambiguationData":[OSD([sQuery(id+"F1.wireOp",EDGE,"E26.MirrorCS")])],"isStart":false});
            var Q15;
            Q15=makeQuery(id+"F2.opExtrude","CAP_EDGE",EDGE,{"disambiguationData":[OSD([sQuery(id+"F1.wireOp",EDGE,"E30.MirrorCS")])],"isStart":false});
            var Q16;
            Q16=makeQuery(id+"F2.opExtrude","CAP_EDGE",EDGE,{"disambiguationData":[OSD([sQuery(id+"F1.wireOp",EDGE,"E29.MirrorCS")])],"isStart":false});
            var Q17;
            Q17=makeQuery(id+"F2.opExtrude","CAP_EDGE",EDGE,{"disambiguationData":[OSD([sQuery(id+"F1.wireOp",EDGE,"E28.MirrorCS")])],"isStart":false});
            var Q18;
            Q18=makeQuery(id+"F2.opExtrude","CAP_EDGE",EDGE,{"disambiguationData":[OSD([sQuery(id+"F1.wireOp",EDGE,"E27.MirrorCS")])],"isStart":false});
            var Q19;
            Q19=makeQuery(id+"F2.opExtrude","CAP_EDGE",EDGE,{"disambiguationData":[OSD([sQuery(id+"F1.wireOp",EDGE,"E25.MirrorCS")])],"isStart":false});
            var Q20;
            Q20=makeQuery(id+"F2.opExtrude","CAP_EDGE",EDGE,{"disambiguationData":[OSD([sQuery(id+"F1.wireOp",EDGE,"E20")])],"isStart":true});
            var Q21;
            Q21=makeQuery(id+"F2.opExtrude","CAP_EDGE",EDGE,{"disambiguationData":[OSD([sQuery(id+"F1.wireOp",EDGE,"E11.MirrorCS")])],"isStart":true});
            var Q22;
            Q22=makeQuery(id+"F2.opExtrude","CAP_EDGE",EDGE,{"disambiguationData":[OSD([sQuery(id+"F1.wireOp",EDGE,"E14")])],"isStart":true});
            var Q23;
            Q23=makeQuery(id+"F2.opExtrude","CAP_EDGE",EDGE,{"disambiguationData":[OSD([sQuery(id+"F1.wireOp",EDGE,"E13")])],"isStart":true});
            var Q24;
            Q24=makeQuery(id+"F2.opExtrude","CAP_EDGE",EDGE,{"disambiguationData":[OSD([sQuery(id+"F1.wireOp",EDGE,"E12.MirrorCS")])],"isStart":true});
            var Q25;
            Q25=makeQuery(id+"F2.opExtrude","CAP_EDGE",EDGE,{"disambiguationData":[OSD([sQuery(id+"F1.wireOp",EDGE,"E19")])],"isStart":true});
            var Q26;
            Q26=makeQuery(id+"F2.opExtrude","CAP_EDGE",EDGE,{"disambiguationData":[OSD([sQuery(id+"F1.wireOp",EDGE,"E15.MirrorCS")])],"isStart":true});
            var Q27;
            Q27=makeQuery(id+"F2.opExtrude","CAP_EDGE",EDGE,{"disambiguationData":[OSD([sQuery(id+"F1.wireOp",EDGE,"E16.MirrorCS")])],"isStart":true});
            var Q28;
            Q28=makeQuery(id+"F2.opExtrude","CAP_EDGE",EDGE,{"disambiguationData":[OSD([sQuery(id+"F1.wireOp",EDGE,"E17.MirrorCS")])],"isStart":true});
            var Q29;
            Q29=makeQuery(id+"F2.opExtrude","CAP_EDGE",EDGE,{"disambiguationData":[OSD([sQuery(id+"F1.wireOp",EDGE,"E18.MirrorCS")])],"isStart":true});
            var Q30;
            Q30=makeQuery(id+"F2.opExtrude","CAP_EDGE",EDGE,{"disambiguationData":[OSD([sQuery(id+"F1.wireOp",EDGE,"E20")])],"isStart":false});
            var Q31;
            Q31=makeQuery(id+"F2.opExtrude","CAP_EDGE",EDGE,{"disambiguationData":[OSD([sQuery(id+"F1.wireOp",EDGE,"E11.MirrorCS")])],"isStart":false});
            var Q32;
            Q32=makeQuery(id+"F2.opExtrude","CAP_EDGE",EDGE,{"disambiguationData":[OSD([sQuery(id+"F1.wireOp",EDGE,"E14")])],"isStart":false});
            var Q33;
            Q33=makeQuery(id+"F2.opExtrude","CAP_EDGE",EDGE,{"disambiguationData":[OSD([sQuery(id+"F1.wireOp",EDGE,"E13")])],"isStart":false});
            var Q34;
            Q34=makeQuery(id+"F2.opExtrude","CAP_EDGE",EDGE,{"disambiguationData":[OSD([sQuery(id+"F1.wireOp",EDGE,"E18.MirrorCS")])],"isStart":false});
            var Q35;
            Q35=makeQuery(id+"F2.opExtrude","CAP_EDGE",EDGE,{"disambiguationData":[OSD([sQuery(id+"F1.wireOp",EDGE,"E17.MirrorCS")])],"isStart":false});
            var Q36;
            Q36=makeQuery(id+"F2.opExtrude","CAP_EDGE",EDGE,{"disambiguationData":[OSD([sQuery(id+"F1.wireOp",EDGE,"E12.MirrorCS")])],"isStart":false});
            var Q37;
            Q37=makeQuery(id+"F2.opExtrude","CAP_EDGE",EDGE,{"disambiguationData":[OSD([sQuery(id+"F1.wireOp",EDGE,"E19")])],"isStart":false});
            var Q38;
            Q38=makeQuery(id+"F2.opExtrude","CAP_EDGE",EDGE,{"disambiguationData":[OSD([sQuery(id+"F1.wireOp",EDGE,"E15.MirrorCS")])],"isStart":false});
            var Q39;
            Q39=makeQuery(id+"F2.opExtrude","CAP_EDGE",EDGE,{"disambiguationData":[OSD([sQuery(id+"F1.wireOp",EDGE,"E16.MirrorCS")])],"isStart":false});
            fillet(context, id + "F11", {"entities" : qUnion([Q0, Q1, Q2, Q3, Q4, Q5, Q6, Q7, Q8, Q9, Q10, Q11, Q12, Q13, Q14, Q15, Q16, Q17, Q18, Q19, Q20, Q21, Q22, Q23, Q24, Q25, Q26, Q27, Q28, Q29, Q30, Q31, Q32, Q33, Q34, Q35, Q36, Q37, Q38, Q39]), "radius" : .5 * mm, "tangentPropagation" : true, "allowEdgeOverflow" : false});
        }
        {
            var Q0;
            Q0=makeQuery(id+"F2.opExtrude","CAP_EDGE",EDGE,{"disambiguationData":[OSD([sQuery(id+"F1.wireOp",EDGE,"E37.left")])],"isStart":false});
            var Q1;
            Q1=makeQuery(id+"F2.opExtrude","CAP_EDGE",EDGE,{"disambiguationData":[OSD([sQuery(id+"F1.wireOp",EDGE,"E37.right")])],"isStart":false});
            var Q2;
            Q2=makeQuery(id+"F2.opExtrude","CAP_EDGE",EDGE,{"disambiguationData":[OSD([sQuery(id+"F1.wireOp",EDGE,"E46.MirrorCS")])],"isStart":false});
            var Q3;
            Q3=makeQuery(id+"F2.opExtrude","CAP_EDGE",EDGE,{"disambiguationData":[OSD([sQuery(id+"F1.wireOp",EDGE,"E47.MirrorCS")])],"isStart":false});
            var Q4;
            Q4=makeQuery(id+"F2.opExtrude","CAP_EDGE",EDGE,{"disambiguationData":[OSD([sQuery(id+"F1.wireOp",EDGE,"E37.left")])],"isStart":true});
            var Q5;
            Q5=makeQuery(id+"F2.opExtrude","CAP_EDGE",EDGE,{"disambiguationData":[OSD([sQuery(id+"F1.wireOp",EDGE,"E37.right")])],"isStart":true});
            var Q6;
            Q6=makeQuery(id+"F2.opExtrude","CAP_EDGE",EDGE,{"disambiguationData":[OSD([sQuery(id+"F1.wireOp",EDGE,"E46.MirrorCS")])],"isStart":true});
            var Q7;
            Q7=makeQuery(id+"F2.opExtrude","CAP_EDGE",EDGE,{"disambiguationData":[OSD([sQuery(id+"F1.wireOp",EDGE,"E47.MirrorCS")])],"isStart":true});
            fillet(context, id + "F12", {"entities" : qUnion([Q0, Q1, Q2, Q3, Q4, Q5, Q6, Q7]), "radius" : .5 * mm, "tangentPropagation" : true, "allowEdgeOverflow" : false});
        }
        {
            var Q0;
            Q0=makeQuery(id+"F2.opExtrude","CAP_EDGE",EDGE,{"disambiguationData":[OSD([sQuery(id+"F1.wireOp",EDGE,"E9.MirrorC")])],"isStart":true});
            var Q1;
            Q1=makeQuery(id+"F2.opExtrude","CAP_EDGE",EDGE,{"disambiguationData":[OSD([sQuery(id+"F1.wireOp",EDGE,"E8.MirrorC")])],"isStart":true});
            var Q2;
            Q2=makeQuery(id+"F2.opExtrude","CAP_EDGE",EDGE,{"disambiguationData":[OSD([sQuery(id+"F1.wireOp",EDGE,"E7.MirrorC")])],"isStart":true});
            var Q3;
            Q3=makeQuery(id+"F2.opExtrude","CAP_EDGE",EDGE,{"disambiguationData":[OSD([sQuery(id+"F1.wireOp",EDGE,"E6")])],"isStart":true});
            fillet(context, id + "F13", {"entities" : qUnion([Q0, Q1, Q2, Q3]), "radius" : .5 * mm, "tangentPropagation" : true, "allowEdgeOverflow" : false});
        }
        {
            var Q0;
            Q0=makeQuery(id+"F2.opExtrude","CAP_EDGE",EDGE,{"disambiguationData":[OSD([sQuery(id+"F1.wireOp",EDGE,"E36")])],"isStart":false});
            var Q1;
            Q1=makeQuery(id+"F2.opExtrude","CAP_EDGE",EDGE,{"disambiguationData":[OSD([sQuery(id+"F1.wireOp",EDGE,"E31")])],"isStart":false});
            var Q2;
            Q2=makeQuery(id+"F2.opExtrude","CAP_EDGE",EDGE,{"disambiguationData":[OSD([sQuery(id+"F1.wireOp",EDGE,"E5")])],"isStart":false});
            var Q3;
            Q3=makeQuery(id+"F2.opExtrude","CAP_EDGE",EDGE,{"disambiguationData":[OSD([sQuery(id+"F1.wireOp",EDGE,"E52.trimOffspring")])],"isStart":false});
            var Q4;
            Q4=makeQuery(id+"F2.opExtrude","CAP_EDGE",EDGE,{"disambiguationData":[OSD([sQuery(id+"F1.wireOp",EDGE,"E56.trimOffspring")])],"isStart":false});
            var Q5;
            Q5=makeQuery(id+"F2.opExtrude","CAP_EDGE",EDGE,{"disambiguationData":[OSD([sQuery(id+"F1.wireOp",EDGE,"E33.MirrorCS")])],"isStart":false});
            var Q6;
            Q6=makeQuery(id+"F2.opExtrude","CAP_EDGE",EDGE,{"disambiguationData":[OSD([sQuery(id+"F1.wireOp",EDGE,"E51")])],"isStart":false});
            var Q7;
            Q7=makeQuery(id+"F2.opExtrude","CAP_EDGE",EDGE,{"disambiguationData":[OSD([sQuery(id+"F1.wireOp",EDGE,"E35.MirrorCS")])],"isStart":false});
            var Q8;
            Q8=makeQuery(id+"F2.opExtrude","CAP_EDGE",EDGE,{"disambiguationData":[OSD([sQuery(id+"F1.wireOp",EDGE,"E34.MirrorCS")])],"isStart":false});
            var Q9;
            Q9=makeQuery(id+"F2.opExtrude","CAP_EDGE",EDGE,{"disambiguationData":[OSD([sQuery(id+"F1.wireOp",EDGE,"E58.trimOffspring")])],"isStart":false});
            var Q10;
            Q10=makeQuery(id+"F2.opExtrude","CAP_EDGE",EDGE,{"disambiguationData":[OSD([sQuery(id+"F1.wireOp",EDGE,"E57.trimOffspring")])],"isStart":false});
            var Q11;
            Q11=makeQuery(id+"F2.opExtrude","CAP_EDGE",EDGE,{"disambiguationData":[OSD([sQuery(id+"F1.wireOp",EDGE,"E32.MirrorCS")])],"isStart":false});
            var Q12;
            Q12=makeQuery(id+"F2.opExtrude","CAP_EDGE",EDGE,{"disambiguationData":[OSD([sQuery(id+"F1.wireOp",EDGE,"E35.MirrorCS")])],"isStart":true});
            var Q13;
            Q13=makeQuery(id+"F2.opExtrude","CAP_EDGE",EDGE,{"disambiguationData":[OSD([sQuery(id+"F1.wireOp",EDGE,"E32.MirrorCS")])],"isStart":true});
            var Q14;
            Q14=makeQuery(id+"F2.opExtrude","CAP_EDGE",EDGE,{"disambiguationData":[OSD([sQuery(id+"F1.wireOp",EDGE,"E57.trimOffspring")])],"isStart":true});
            var Q15;
            Q15=makeQuery(id+"F2.opExtrude","CAP_EDGE",EDGE,{"disambiguationData":[OSD([sQuery(id+"F1.wireOp",EDGE,"E58.trimOffspring")])],"isStart":true});
            var Q16;
            Q16=makeQuery(id+"F2.opExtrude","CAP_EDGE",EDGE,{"disambiguationData":[OSD([sQuery(id+"F1.wireOp",EDGE,"E3.MirrorC")])],"isStart":true});
            var Q17;
            Q17=makeQuery(id+"F2.opExtrude","CAP_EDGE",EDGE,{"disambiguationData":[OSD([sQuery(id+"F1.wireOp",EDGE,"E34.MirrorCS")])],"isStart":true});
            var Q18;
            Q18=makeQuery(id+"F2.opExtrude","CAP_EDGE",EDGE,{"disambiguationData":[OSD([sQuery(id+"F1.wireOp",EDGE,"E4.MirrorC")])],"isStart":true});
            var Q19;
            {var subQ0=sQuery(id+"F1.wireOp",EDGE,"E37.left");Q19=makeQuery(id+"F12.opFillet","BLEND_EDGE",EDGE,{"blendedFrom":[makeQuery(id+"F2.opExtrude","CAP_EDGE",EDGE,{"disambiguationData":[OSD([subQ0])],"isStart":true}),makeQuery(id+"F2.opExtrude","CAP_FACE",FACE,{"disambiguationData":[OSD([sQuery(id+"F1.wireOp",EDGE,"E1"),sQuery(id+"F1.wireOp",EDGE,"E2.MirrorC"),sQuery(id+"F1.wireOp",EDGE,"E3.MirrorC"),sQuery(id+"F1.wireOp",EDGE,"E4.MirrorC"),sQuery(id+"F1.wireOp",EDGE,"E5"),sQuery(id+"F1.wireOp",EDGE,"E6"),sQuery(id+"F1.wireOp",EDGE,"E7.MirrorC"),sQuery(id+"F1.wireOp",EDGE,"E8.MirrorC"),sQuery(id+"F1.wireOp",EDGE,"E9.MirrorC"),sQuery(id+"F1.wireOp",EDGE,"E11.MirrorCS"),sQuery(id+"F1.wireOp",EDGE,"E12.MirrorCS"),sQuery(id+"F1.wireOp",EDGE,"E13"),sQuery(id+"F1.wireOp",EDGE,"E14"),sQuery(id+"F1.wireOp",EDGE,"E15.MirrorCS"),sQuery(id+"F1.wireOp",EDGE,"E16.MirrorCS"),sQuery(id+"F1.wireOp",EDGE,"E17.MirrorCS"),sQuery(id+"F1.wireOp",EDGE,"E18.MirrorCS"),sQuery(id+"F1.wireOp",EDGE,"E19"),sQuery(id+"F1.wireOp",EDGE,"E20"),sQuery(id+"F1.wireOp",EDGE,"E21.MirrorCS"),sQuery(id+"F1.wireOp",EDGE,"E22.MirrorCS"),sQuery(id+"F1.wireOp",EDGE,"E23.MirrorCS"),sQuery(id+"F1.wireOp",EDGE,"E24.MirrorCS"),sQuery(id+"F1.wireOp",EDGE,"E25.MirrorCS"),sQuery(id+"F1.wireOp",EDGE,"E26.MirrorCS"),sQuery(id+"F1.wireOp",EDGE,"E27.MirrorCS"),sQuery(id+"F1.wireOp",EDGE,"E28.MirrorCS"),sQuery(id+"F1.wireOp",EDGE,"E29.MirrorCS"),sQuery(id+"F1.wireOp",EDGE,"E30.MirrorCS"),sQuery(id+"F1.wireOp",EDGE,"E31"),sQuery(id+"F1.wireOp",EDGE,"E32.MirrorCS"),sQuery(id+"F1.wireOp",EDGE,"E33.MirrorCS"),sQuery(id+"F1.wireOp",EDGE,"E34.MirrorCS"),sQuery(id+"F1.wireOp",EDGE,"E35.MirrorCS"),sQuery(id+"F1.wireOp",EDGE,"E36"),sQuery(id+"F1.wireOp",EDGE,"E37.bottom"),sQuery(id+"F1.wireOp",EDGE,"E37.top"),subQ0,sQuery(id+"F1.wireOp",EDGE,"E37.right"),sQuery(id+"F1.wireOp",EDGE,"E39.filletArc"),sQuery(id+"F1.wireOp",EDGE,"E40.filletArc"),sQuery(id+"F1.wireOp",EDGE,"E41.filletArc"),sQuery(id+"F1.wireOp",EDGE,"E42.filletArc"),sQuery(id+"F1.wireOp",EDGE,"E43.MirrorCS"),sQuery(id+"F1.wireOp",EDGE,"E44.MirrorCS"),sQuery(id+"F1.wireOp",EDGE,"E45.MirrorCS"),sQuery(id+"F1.wireOp",EDGE,"E46.MirrorCS"),sQuery(id+"F1.wireOp",EDGE,"E47.MirrorCS"),sQuery(id+"F1.wireOp",EDGE,"E48.MirrorCS"),sQuery(id+"F1.wireOp",EDGE,"E49.MirrorCS"),sQuery(id+"F1.wireOp",EDGE,"E50.MirrorCS"),sQuery(id+"F1.wireOp",EDGE,"E51"),sQuery(id+"F1.wireOp",EDGE,"E52.trimOffspring"),sQuery(id+"F1.wireOp",EDGE,"E53"),sQuery(id+"F1.wireOp",EDGE,"b30a117b-d75a-4502-b387-7b125c7515d1.trimOffspring"),sQuery(id+"F1.wireOp",EDGE,"E54"),sQuery(id+"F1.wireOp",EDGE,"E55.MirrorCS"),sQuery(id+"F1.wireOp",EDGE,"E56.trimOffspring"),sQuery(id+"F1.wireOp",EDGE,"E57.trimOffspring"),sQuery(id+"F1.wireOp",EDGE,"E58.trimOffspring"),sQuery(id+"F1.wireOp",EDGE,"XfeBEER9-2g1J-kN3v-mQVF-R0Wur47D0a7y"),sQuery(id+"F1.wireOp",EDGE,"cj9tdcR5-JuoR-tGsP-MGoO-S5KOOCOVeEPM"),sQuery(id+"F1.wireOp",EDGE,"E59.MirrorCS"),sQuery(id+"F1.wireOp",EDGE,"E60.MirrorCS"),sQuery(id+"F1.wireOp",EDGE,"c64e98b8-e32c-4987-8556-cb4b40954b380.MirrorCS"),sQuery(id+"F1.wireOp",EDGE,"E61.MirrorCS"),sQuery(id+"F1.wireOp",EDGE,"E62.MirrorCS"),sQuery(id+"F1.wireOp",EDGE,"E63.MirrorCS"),sQuery(id+"F1.wireOp",EDGE,"E64.MirrorCS"),sQuery(id+"F1.wireOp",EDGE,"bcf6c320-8a54-4c53-9ffd-94a113f5b3590.MirrorCS"),sQuery(id+"F1.wireOp",EDGE,"c17ce9da-a2d4-493a-92bd-da0e6258ab510.MirrorCS"),sQuery(id+"F1.wireOp",EDGE,"E65.MirrorCS"),sQuery(id+"F1.wireOp",EDGE,"E66.MirrorCS"),sQuery(id+"F1.wireOp",EDGE,"E67.MirrorCS"),sQuery(id+"F1.wireOp",EDGE,"eab108b2-96d9-45b4-925c-b77b0fad8b6b0.MirrorCS"),sQuery(id+"F1.wireOp",EDGE,"861f5b8e-cbd1-41e1-b2bb-9c07049055a20.MirrorCS")])],"isStart":true})],"blendedInto":[makeQuery(id+"F2.opExtrude","CAP_FACE",FACE,{"disambiguationData":[OSD([sQuery(id+"F1.wireOp",EDGE,"E1"),sQuery(id+"F1.wireOp",EDGE,"E2.MirrorC"),sQuery(id+"F1.wireOp",EDGE,"E3.MirrorC"),sQuery(id+"F1.wireOp",EDGE,"E4.MirrorC"),sQuery(id+"F1.wireOp",EDGE,"E5"),sQuery(id+"F1.wireOp",EDGE,"E6"),sQuery(id+"F1.wireOp",EDGE,"E7.MirrorC"),sQuery(id+"F1.wireOp",EDGE,"E8.MirrorC"),sQuery(id+"F1.wireOp",EDGE,"E9.MirrorC"),sQuery(id+"F1.wireOp",EDGE,"E11.MirrorCS"),sQuery(id+"F1.wireOp",EDGE,"E12.MirrorCS"),sQuery(id+"F1.wireOp",EDGE,"E13"),sQuery(id+"F1.wireOp",EDGE,"E14"),sQuery(id+"F1.wireOp",EDGE,"E15.MirrorCS"),sQuery(id+"F1.wireOp",EDGE,"E16.MirrorCS"),sQuery(id+"F1.wireOp",EDGE,"E17.MirrorCS"),sQuery(id+"F1.wireOp",EDGE,"E18.MirrorCS"),sQuery(id+"F1.wireOp",EDGE,"E19"),sQuery(id+"F1.wireOp",EDGE,"E20"),sQuery(id+"F1.wireOp",EDGE,"E21.MirrorCS"),sQuery(id+"F1.wireOp",EDGE,"E22.MirrorCS"),sQuery(id+"F1.wireOp",EDGE,"E23.MirrorCS"),sQuery(id+"F1.wireOp",EDGE,"E24.MirrorCS"),sQuery(id+"F1.wireOp",EDGE,"E25.MirrorCS"),sQuery(id+"F1.wireOp",EDGE,"E26.MirrorCS"),sQuery(id+"F1.wireOp",EDGE,"E27.MirrorCS"),sQuery(id+"F1.wireOp",EDGE,"E28.MirrorCS"),sQuery(id+"F1.wireOp",EDGE,"E29.MirrorCS"),sQuery(id+"F1.wireOp",EDGE,"E30.MirrorCS"),sQuery(id+"F1.wireOp",EDGE,"E31"),sQuery(id+"F1.wireOp",EDGE,"E32.MirrorCS"),sQuery(id+"F1.wireOp",EDGE,"E33.MirrorCS"),sQuery(id+"F1.wireOp",EDGE,"E34.MirrorCS"),sQuery(id+"F1.wireOp",EDGE,"E35.MirrorCS"),sQuery(id+"F1.wireOp",EDGE,"E36"),sQuery(id+"F1.wireOp",EDGE,"E37.bottom"),sQuery(id+"F1.wireOp",EDGE,"E37.top"),subQ0,sQuery(id+"F1.wireOp",EDGE,"E37.right"),sQuery(id+"F1.wireOp",EDGE,"E39.filletArc"),sQuery(id+"F1.wireOp",EDGE,"E40.filletArc"),sQuery(id+"F1.wireOp",EDGE,"E41.filletArc"),sQuery(id+"F1.wireOp",EDGE,"E42.filletArc"),sQuery(id+"F1.wireOp",EDGE,"E43.MirrorCS"),sQuery(id+"F1.wireOp",EDGE,"E44.MirrorCS"),sQuery(id+"F1.wireOp",EDGE,"E45.MirrorCS"),sQuery(id+"F1.wireOp",EDGE,"E46.MirrorCS"),sQuery(id+"F1.wireOp",EDGE,"E47.MirrorCS"),sQuery(id+"F1.wireOp",EDGE,"E48.MirrorCS"),sQuery(id+"F1.wireOp",EDGE,"E49.MirrorCS"),sQuery(id+"F1.wireOp",EDGE,"E50.MirrorCS"),sQuery(id+"F1.wireOp",EDGE,"E51"),sQuery(id+"F1.wireOp",EDGE,"E52.trimOffspring"),sQuery(id+"F1.wireOp",EDGE,"E53"),sQuery(id+"F1.wireOp",EDGE,"b30a117b-d75a-4502-b387-7b125c7515d1.trimOffspring"),sQuery(id+"F1.wireOp",EDGE,"E54"),sQuery(id+"F1.wireOp",EDGE,"E55.MirrorCS"),sQuery(id+"F1.wireOp",EDGE,"E56.trimOffspring"),sQuery(id+"F1.wireOp",EDGE,"E57.trimOffspring"),sQuery(id+"F1.wireOp",EDGE,"E58.trimOffspring"),sQuery(id+"F1.wireOp",EDGE,"XfeBEER9-2g1J-kN3v-mQVF-R0Wur47D0a7y"),sQuery(id+"F1.wireOp",EDGE,"cj9tdcR5-JuoR-tGsP-MGoO-S5KOOCOVeEPM"),sQuery(id+"F1.wireOp",EDGE,"E59.MirrorCS"),sQuery(id+"F1.wireOp",EDGE,"E60.MirrorCS"),sQuery(id+"F1.wireOp",EDGE,"c64e98b8-e32c-4987-8556-cb4b40954b380.MirrorCS"),sQuery(id+"F1.wireOp",EDGE,"E61.MirrorCS"),sQuery(id+"F1.wireOp",EDGE,"E62.MirrorCS"),sQuery(id+"F1.wireOp",EDGE,"E63.MirrorCS"),sQuery(id+"F1.wireOp",EDGE,"E64.MirrorCS"),sQuery(id+"F1.wireOp",EDGE,"bcf6c320-8a54-4c53-9ffd-94a113f5b3590.MirrorCS"),sQuery(id+"F1.wireOp",EDGE,"c17ce9da-a2d4-493a-92bd-da0e6258ab510.MirrorCS"),sQuery(id+"F1.wireOp",EDGE,"E65.MirrorCS"),sQuery(id+"F1.wireOp",EDGE,"E66.MirrorCS"),sQuery(id+"F1.wireOp",EDGE,"E67.MirrorCS"),sQuery(id+"F1.wireOp",EDGE,"eab108b2-96d9-45b4-925c-b77b0fad8b6b0.MirrorCS"),sQuery(id+"F1.wireOp",EDGE,"861f5b8e-cbd1-41e1-b2bb-9c07049055a20.MirrorCS")])],"isStart":true})]});}
            var Q20;
            Q20=makeQuery(id+"F2.opExtrude","CAP_EDGE",EDGE,{"disambiguationData":[OSD([sQuery(id+"F1.wireOp",EDGE,"E51")])],"isStart":true});
            var Q21;
            Q21=makeQuery(id+"F2.opExtrude","CAP_EDGE",EDGE,{"disambiguationData":[OSD([sQuery(id+"F1.wireOp",EDGE,"E36")])],"isStart":true});
            var Q22;
            Q22=makeQuery(id+"F2.opExtrude","CAP_EDGE",EDGE,{"disambiguationData":[OSD([sQuery(id+"F1.wireOp",EDGE,"E33.MirrorCS")])],"isStart":true});
            var Q23;
            Q23=makeQuery(id+"F2.opExtrude","CAP_EDGE",EDGE,{"disambiguationData":[OSD([sQuery(id+"F1.wireOp",EDGE,"E31")])],"isStart":true});
            var Q24;
            Q24=makeQuery(id+"F2.opExtrude","CAP_EDGE",EDGE,{"disambiguationData":[OSD([sQuery(id+"F1.wireOp",EDGE,"E1")])],"isStart":true});
            var Q25;
            Q25=makeQuery(id+"F2.opExtrude","CAP_EDGE",EDGE,{"disambiguationData":[OSD([sQuery(id+"F1.wireOp",EDGE,"E5")])],"isStart":true});
            var Q26;
            Q26=makeQuery(id+"F2.opExtrude","CAP_EDGE",EDGE,{"disambiguationData":[OSD([sQuery(id+"F1.wireOp",EDGE,"E52.trimOffspring")])],"isStart":true});
            var Q27;
            Q27=makeQuery(id+"F2.opExtrude","CAP_EDGE",EDGE,{"disambiguationData":[OSD([sQuery(id+"F1.wireOp",EDGE,"E56.trimOffspring")])],"isStart":true});
            var Q28;
            Q28=makeQuery(id+"F2.opExtrude","CAP_EDGE",EDGE,{"disambiguationData":[OSD([sQuery(id+"F1.wireOp",EDGE,"E2.MirrorC")])],"isStart":true});
            fillet(context, id + "F14", {"entities" : qUnion([Q0, Q1, Q2, Q3, Q4, Q5, Q6, Q7, Q8, Q9, Q10, Q11, Q12, Q13, Q14, Q15, Q16, Q17, Q18, Q19, Q20, Q21, Q22, Q23, Q24, Q25, Q26, Q27, Q28]), "radius" : .5 * mm, "tangentPropagation" : true, "allowEdgeOverflow" : false});
        }
        {
            var Q0;
            Q0=makeQuery(id+"F2.opExtrude","CAP_FACE",FACE,{"disambiguationData":[OSD([sQuery(id+"F1.wireOp",EDGE,"E1"),sQuery(id+"F1.wireOp",EDGE,"E2.MirrorC"),sQuery(id+"F1.wireOp",EDGE,"E3.MirrorC"),sQuery(id+"F1.wireOp",EDGE,"E4.MirrorC"),sQuery(id+"F1.wireOp",EDGE,"E5"),sQuery(id+"F1.wireOp",EDGE,"E6"),sQuery(id+"F1.wireOp",EDGE,"E7.MirrorC"),sQuery(id+"F1.wireOp",EDGE,"E8.MirrorC"),sQuery(id+"F1.wireOp",EDGE,"E9.MirrorC"),sQuery(id+"F1.wireOp",EDGE,"E11.MirrorCS"),sQuery(id+"F1.wireOp",EDGE,"E12.MirrorCS"),sQuery(id+"F1.wireOp",EDGE,"E13"),sQuery(id+"F1.wireOp",EDGE,"E14"),sQuery(id+"F1.wireOp",EDGE,"E15.MirrorCS"),sQuery(id+"F1.wireOp",EDGE,"E16.MirrorCS"),sQuery(id+"F1.wireOp",EDGE,"E17.MirrorCS"),sQuery(id+"F1.wireOp",EDGE,"E18.MirrorCS"),sQuery(id+"F1.wireOp",EDGE,"E19"),sQuery(id+"F1.wireOp",EDGE,"E20"),sQuery(id+"F1.wireOp",EDGE,"E21.MirrorCS"),sQuery(id+"F1.wireOp",EDGE,"E22.MirrorCS"),sQuery(id+"F1.wireOp",EDGE,"E23.MirrorCS"),sQuery(id+"F1.wireOp",EDGE,"E24.MirrorCS"),sQuery(id+"F1.wireOp",EDGE,"E25.MirrorCS"),sQuery(id+"F1.wireOp",EDGE,"E26.MirrorCS"),sQuery(id+"F1.wireOp",EDGE,"E27.MirrorCS"),sQuery(id+"F1.wireOp",EDGE,"E28.MirrorCS"),sQuery(id+"F1.wireOp",EDGE,"E29.MirrorCS"),sQuery(id+"F1.wireOp",EDGE,"E30.MirrorCS"),sQuery(id+"F1.wireOp",EDGE,"E31"),sQuery(id+"F1.wireOp",EDGE,"E32.MirrorCS"),sQuery(id+"F1.wireOp",EDGE,"E33.MirrorCS"),sQuery(id+"F1.wireOp",EDGE,"E34.MirrorCS"),sQuery(id+"F1.wireOp",EDGE,"E35.MirrorCS"),sQuery(id+"F1.wireOp",EDGE,"E36"),sQuery(id+"F1.wireOp",EDGE,"E37.bottom"),sQuery(id+"F1.wireOp",EDGE,"E37.top"),sQuery(id+"F1.wireOp",EDGE,"E37.left"),sQuery(id+"F1.wireOp",EDGE,"E37.right"),sQuery(id+"F1.wireOp",EDGE,"E39.filletArc"),sQuery(id+"F1.wireOp",EDGE,"E40.filletArc"),sQuery(id+"F1.wireOp",EDGE,"E41.filletArc"),sQuery(id+"F1.wireOp",EDGE,"E42.filletArc"),sQuery(id+"F1.wireOp",EDGE,"E43.MirrorCS"),sQuery(id+"F1.wireOp",EDGE,"E44.MirrorCS"),sQuery(id+"F1.wireOp",EDGE,"E45.MirrorCS"),sQuery(id+"F1.wireOp",EDGE,"E46.MirrorCS"),sQuery(id+"F1.wireOp",EDGE,"E47.MirrorCS"),sQuery(id+"F1.wireOp",EDGE,"E48.MirrorCS"),sQuery(id+"F1.wireOp",EDGE,"E49.MirrorCS"),sQuery(id+"F1.wireOp",EDGE,"E50.MirrorCS"),sQuery(id+"F1.wireOp",EDGE,"E51"),sQuery(id+"F1.wireOp",EDGE,"E52.trimOffspring"),sQuery(id+"F1.wireOp",EDGE,"E53"),sQuery(id+"F1.wireOp",EDGE,"b30a117b-d75a-4502-b387-7b125c7515d1.trimOffspring"),sQuery(id+"F1.wireOp",EDGE,"E54"),sQuery(id+"F1.wireOp",EDGE,"E55.MirrorCS"),sQuery(id+"F1.wireOp",EDGE,"E56.trimOffspring"),sQuery(id+"F1.wireOp",EDGE,"E57.trimOffspring"),sQuery(id+"F1.wireOp",EDGE,"E58.trimOffspring"),sQuery(id+"F1.wireOp",EDGE,"XfeBEER9-2g1J-kN3v-mQVF-R0Wur47D0a7y"),sQuery(id+"F1.wireOp",EDGE,"cj9tdcR5-JuoR-tGsP-MGoO-S5KOOCOVeEPM"),sQuery(id+"F1.wireOp",EDGE,"E59.MirrorCS"),sQuery(id+"F1.wireOp",EDGE,"E60.MirrorCS"),sQuery(id+"F1.wireOp",EDGE,"c64e98b8-e32c-4987-8556-cb4b40954b380.MirrorCS"),sQuery(id+"F1.wireOp",EDGE,"E61.MirrorCS"),sQuery(id+"F1.wireOp",EDGE,"E62.MirrorCS"),sQuery(id+"F1.wireOp",EDGE,"E63.MirrorCS"),sQuery(id+"F1.wireOp",EDGE,"E64.MirrorCS"),sQuery(id+"F1.wireOp",EDGE,"bcf6c320-8a54-4c53-9ffd-94a113f5b3590.MirrorCS"),sQuery(id+"F1.wireOp",EDGE,"c17ce9da-a2d4-493a-92bd-da0e6258ab510.MirrorCS"),sQuery(id+"F1.wireOp",EDGE,"E65.MirrorCS"),sQuery(id+"F1.wireOp",EDGE,"E66.MirrorCS"),sQuery(id+"F1.wireOp",EDGE,"E67.MirrorCS"),sQuery(id+"F1.wireOp",EDGE,"eab108b2-96d9-45b4-925c-b77b0fad8b6b0.MirrorCS"),sQuery(id+"F1.wireOp",EDGE,"861f5b8e-cbd1-41e1-b2bb-9c07049055a20.MirrorCS")])],"isStart":false});
            var sketch = newSketch(context, id + "F15", { "sketchPlane" : qUnion([Q0])});
            skPoint(sketch, "E107", {"position": v(17.08, -38.68) * mm});
            skPoint(sketch, "E108", {"position": v(19.36, -40.8) * mm});
            skArc(sketch, "E109", {"start": v(17.08, -38.68) * mm, "mid": v(18.16, -39.8) * mm, "end": v(19.36, -40.8) * mm});
            skPoint(sketch, "E110", {"position": v(17.34, -42.89) * mm});
            skPoint(sketch, "E111", {"position": v(15.3, -41.07) * mm});
            skArc(sketch, "E112", {"start": v(17.34, -42.89) * mm, "mid": v(16.68, -41.58) * mm, "end": v(15.3, -41.07) * mm});
            skPoint(sketch, "E113.right.end.orphan", {"position": v(13.51, -37.55) * mm});
            skArc(sketch, "E114", {"start": v(17.08, -38.68) * mm, "mid": v(14.83, -38.87) * mm, "end": v(15.3, -41.07) * mm});
            skArc(sketch, "E115", {"start": v(17.34, -42.89) * mm, "mid": v(19.54, -43.3) * mm, "end": v(19.71, -41.08) * mm});
            skPoint(sketch, "E116", {"position": v(19.71, -41.08) * mm});
            skLineSegment(sketch, "E117", {"start": v(19.71, -41.08) * mm, "end": v(19.36, -40.8) * mm});
            skArc(sketch, "E118.MirrorCS", {"start": v(-17.08, -38.68) * mm, "mid": v(-14.83, -38.87) * mm, "end": v(-15.3, -41.07) * mm});
            skArc(sketch, "E119.MirrorCS", {"start": v(-17.08, -38.68) * mm, "mid": v(-18.16, -39.8) * mm, "end": v(-19.36, -40.8) * mm});
            skLineSegment(sketch, "E120.MirrorCS", {"start": v(-19.71, -41.08) * mm, "end": v(-19.36, -40.8) * mm});
            skArc(sketch, "E121.MirrorCS", {"start": v(-17.34, -42.89) * mm, "mid": v(-19.54, -43.3) * mm, "end": v(-19.71, -41.08) * mm});
            skArc(sketch, "E122.MirrorCS", {"start": v(-17.34, -42.89) * mm, "mid": v(-16.68, -41.58) * mm, "end": v(-15.3, -41.07) * mm});
            skArc(sketch, "E123.MirrorCS", {"start": v(-17.08, 38.68) * mm, "mid": v(-14.83, 38.87) * mm, "end": v(-15.3, 41.07) * mm});
            skArc(sketch, "E124.MirrorCS", {"start": v(-17.34, 42.89) * mm, "mid": v(-16.68, 41.58) * mm, "end": v(-15.3, 41.07) * mm});
            skArc(sketch, "E125.MirrorCS", {"start": v(-17.34, 42.89) * mm, "mid": v(-19.54, 43.3) * mm, "end": v(-19.71, 41.08) * mm});
            skArc(sketch, "E126.MirrorCS", {"start": v(-17.08, 38.68) * mm, "mid": v(-18.16, 39.8) * mm, "end": v(-19.36, 40.8) * mm});
            skLineSegment(sketch, "E127.MirrorCS", {"start": v(-19.71, 41.08) * mm, "end": v(-19.36, 40.8) * mm});
            skArc(sketch, "E128.MirrorCS", {"start": v(17.08, 38.68) * mm, "mid": v(18.16, 39.8) * mm, "end": v(19.36, 40.8) * mm});
            skArc(sketch, "E129.MirrorCS", {"start": v(17.08, 38.68) * mm, "mid": v(14.83, 38.87) * mm, "end": v(15.3, 41.07) * mm});
            skArc(sketch, "E130.MirrorCS", {"start": v(17.34, 42.89) * mm, "mid": v(16.68, 41.58) * mm, "end": v(15.3, 41.07) * mm});
            skArc(sketch, "E131.MirrorCS", {"start": v(17.34, 42.89) * mm, "mid": v(19.54, 43.3) * mm, "end": v(19.71, 41.08) * mm});
            skLineSegment(sketch, "E132.MirrorCS", {"start": v(19.71, 41.08) * mm, "end": v(19.36, 40.8) * mm});
            skLineSegment(sketch, "E133", {"start": v(16.68, -41.58) * mm, "end": v(18.16, -39.8) * mm, "construction": true});
            skSolve(sketch);
        }
        {
            var Q0;
            Q0=qSketchRegion(id+"F15",true);
            extrude(context, id + "F16", {"entities" : qUnion([Q0]), "operationType" : NewBodyOperationType.ADD, "depth" : 1 * mm});
        }
        {
            var Q0;
            Q0=makeQuery(id+"F16.opExtrude","CAP_EDGE",EDGE,{"disambiguationData":[OSD([sQuery(id+"F15.wireOp",EDGE,"E112")])],"isStart":false});
            var Q1;
            Q1=makeQuery(id+"F16.opExtrude","CAP_EDGE",EDGE,{"disambiguationData":[OSD([sQuery(id+"F15.wireOp",EDGE,"E114")])],"isStart":false});
            var Q2;
            Q2=makeQuery(id+"F16.opExtrude","CAP_EDGE",EDGE,{"disambiguationData":[OSD([sQuery(id+"F15.wireOp",EDGE,"E109")])],"isStart":false});
            var Q3;
            Q3=makeQuery(id+"F16.opExtrude","CAP_EDGE",EDGE,{"disambiguationData":[OSD([sQuery(id+"F15.wireOp",EDGE,"E115")])],"isStart":false});
            var Q4;
            Q4=makeQuery(id+"F16.opExtrude","CAP_EDGE",EDGE,{"disambiguationData":[OSD([sQuery(id+"F15.wireOp",EDGE,"E117")])],"isStart":false});
            var Q5;
            Q5=makeQuery(id+"F16.opExtrude","CAP_EDGE",EDGE,{"disambiguationData":[OSD([sQuery(id+"F15.wireOp",EDGE,"E121.MirrorCS")])],"isStart":false});
            var Q6;
            Q6=makeQuery(id+"F16.opExtrude","CAP_EDGE",EDGE,{"disambiguationData":[OSD([sQuery(id+"F15.wireOp",EDGE,"E122.MirrorCS")])],"isStart":false});
            var Q7;
            Q7=makeQuery(id+"F16.opExtrude","CAP_EDGE",EDGE,{"disambiguationData":[OSD([sQuery(id+"F15.wireOp",EDGE,"E118.MirrorCS")])],"isStart":false});
            var Q8;
            Q8=makeQuery(id+"F16.opExtrude","CAP_EDGE",EDGE,{"disambiguationData":[OSD([sQuery(id+"F15.wireOp",EDGE,"E119.MirrorCS")])],"isStart":false});
            var Q9;
            Q9=makeQuery(id+"F16.opExtrude","CAP_EDGE",EDGE,{"disambiguationData":[OSD([sQuery(id+"F15.wireOp",EDGE,"E120.MirrorCS")])],"isStart":false});
            var Q10;
            Q10=makeQuery(id+"F16.opExtrude","CAP_EDGE",EDGE,{"disambiguationData":[OSD([sQuery(id+"F15.wireOp",EDGE,"E126.MirrorCS")])],"isStart":false});
            var Q11;
            Q11=makeQuery(id+"F16.opExtrude","CAP_EDGE",EDGE,{"disambiguationData":[OSD([sQuery(id+"F15.wireOp",EDGE,"E127.MirrorCS")])],"isStart":false});
            var Q12;
            Q12=makeQuery(id+"F16.opExtrude","CAP_EDGE",EDGE,{"disambiguationData":[OSD([sQuery(id+"F15.wireOp",EDGE,"E125.MirrorCS")])],"isStart":false});
            var Q13;
            Q13=makeQuery(id+"F16.opExtrude","CAP_EDGE",EDGE,{"disambiguationData":[OSD([sQuery(id+"F15.wireOp",EDGE,"E124.MirrorCS")])],"isStart":false});
            var Q14;
            Q14=makeQuery(id+"F16.opExtrude","CAP_EDGE",EDGE,{"disambiguationData":[OSD([sQuery(id+"F15.wireOp",EDGE,"E123.MirrorCS")])],"isStart":false});
            var Q15;
            Q15=makeQuery(id+"F16.opExtrude","CAP_EDGE",EDGE,{"disambiguationData":[OSD([sQuery(id+"F15.wireOp",EDGE,"E128.MirrorCS")])],"isStart":false});
            var Q16;
            Q16=makeQuery(id+"F16.opExtrude","CAP_EDGE",EDGE,{"disambiguationData":[OSD([sQuery(id+"F15.wireOp",EDGE,"E132.MirrorCS")])],"isStart":false});
            var Q17;
            Q17=makeQuery(id+"F16.opExtrude","CAP_EDGE",EDGE,{"disambiguationData":[OSD([sQuery(id+"F15.wireOp",EDGE,"E131.MirrorCS")])],"isStart":false});
            var Q18;
            Q18=makeQuery(id+"F16.opExtrude","CAP_EDGE",EDGE,{"disambiguationData":[OSD([sQuery(id+"F15.wireOp",EDGE,"E130.MirrorCS")])],"isStart":false});
            var Q19;
            Q19=makeQuery(id+"F16.opExtrude","CAP_EDGE",EDGE,{"disambiguationData":[OSD([sQuery(id+"F15.wireOp",EDGE,"E129.MirrorCS")])],"isStart":false});
            fillet(context, id + "F17", {"entities" : qUnion([Q0, Q1, Q2, Q3, Q4, Q5, Q6, Q7, Q8, Q9, Q10, Q11, Q12, Q13, Q14, Q15, Q16, Q17, Q18, Q19]), "radius" : 1 * mm, "tangentPropagation" : true, "allowEdgeOverflow" : false});
        }
    });
